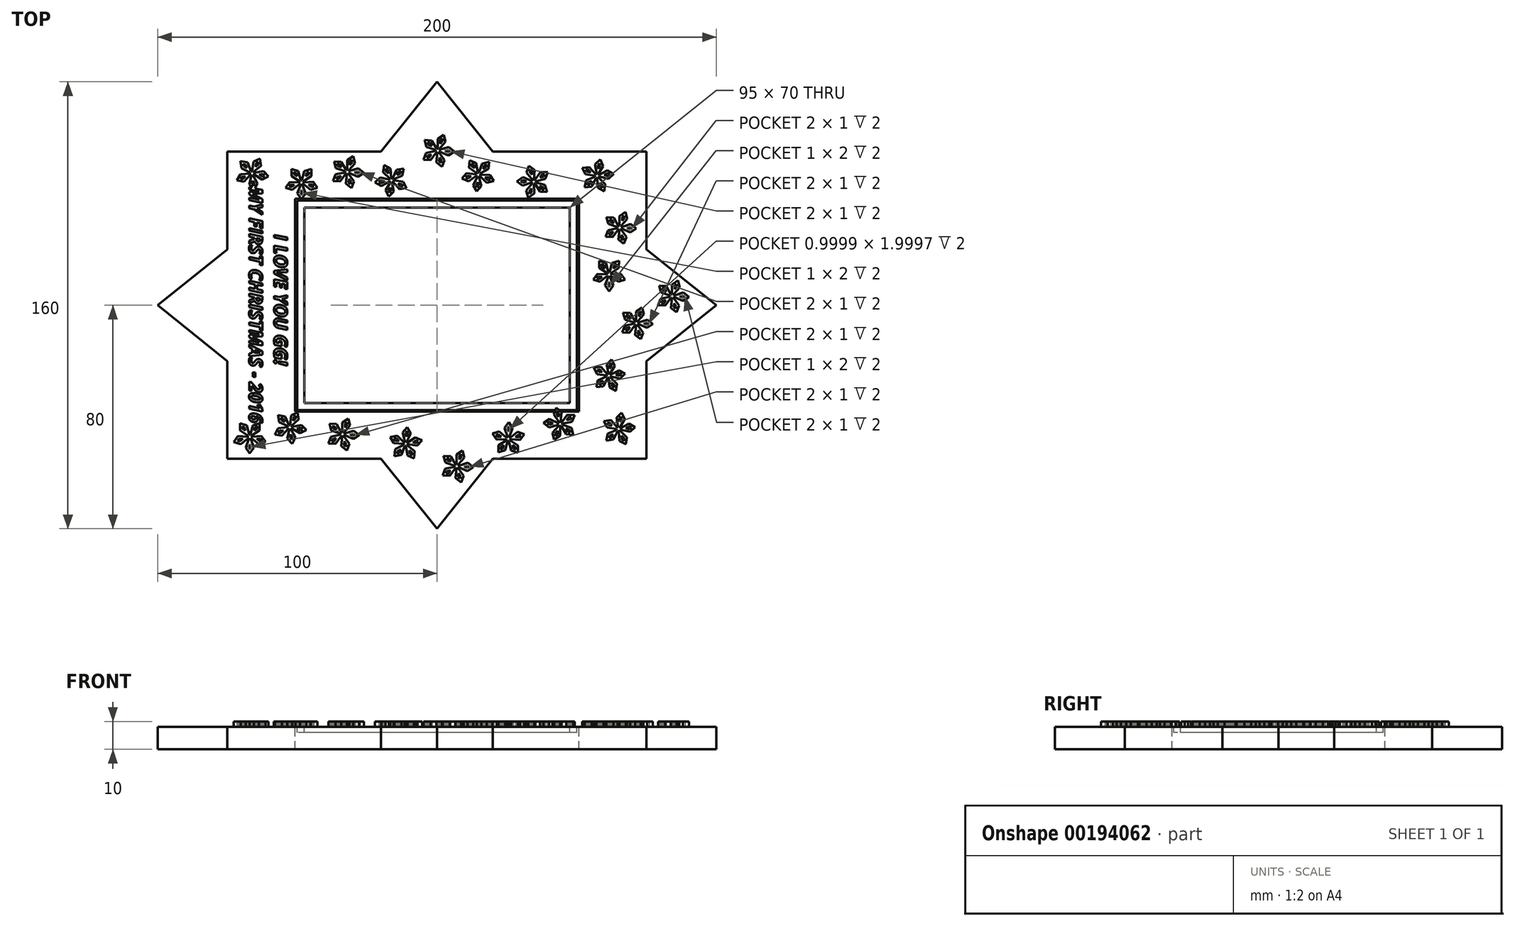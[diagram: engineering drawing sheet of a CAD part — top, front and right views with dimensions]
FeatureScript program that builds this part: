
annotation { "Feature Type Name" : "Feature", "Feature Type Description" : "" }
export const myFeature = defineFeature(function(context is Context, id is Id, definition is map)
    precondition{}
    {
        {
            var Q0;
            Q0=qCreatedBy(makeId("Top.planeOp"),FACE);
            var sketch = newSketch(context, id + "F0", { "sketchPlane" : qUnion([Q0])});
            skLineSegment(sketch, "E0.bottom", {"start": v(75, 55) * mm, "end": v(20, 55) * mm});
            skLineSegment(sketch, "E0.top", {"start": v(75, -55) * mm, "end": v(20, -55) * mm});
            skLineSegment(sketch, "E0.left", {"start": v(75, 55) * mm, "end": v(75, 20) * mm});
            skLineSegment(sketch, "E0.right", {"start": v(-75, 55) * mm, "end": v(-75, 20) * mm});
            skLineSegment(sketch, "E1", {"start": v(75, 20) * mm, "end": v(100, 0) * mm});
            skLineSegment(sketch, "E2", {"start": v(-20, 55) * mm, "end": v(0, 80) * mm});
            skLineSegment(sketch, "E3", {"start": v(0, 80) * mm, "end": v(20, 55) * mm});
            skLineSegment(sketch, "E4.MirrorCS", {"start": v(-20, -55) * mm, "end": v(0, -80) * mm});
            skLineSegment(sketch, "E5.MirrorCS", {"start": v(0, -80) * mm, "end": v(20, -55) * mm});
            skLineSegment(sketch, "E6.MirrorCS", {"start": v(75, -20) * mm, "end": v(100, 0) * mm});
            skLineSegment(sketch, "E7.MirrorCS", {"start": v(-75, 20) * mm, "end": v(-100, 0) * mm});
            skLineSegment(sketch, "E8.MirrorCS", {"start": v(-75, -20) * mm, "end": v(-100, 0) * mm});
            skLineSegment(sketch, "E9.trimOffspring", {"start": v(-75, -20) * mm, "end": v(-75, -55) * mm});
            skLineSegment(sketch, "E10.trimOffspring", {"start": v(75, -20) * mm, "end": v(75, -55) * mm});
            skLineSegment(sketch, "E11.trimOffspring", {"start": v(-20, -55) * mm, "end": v(-75, -55) * mm});
            skLineSegment(sketch, "E12.trimOffspring", {"start": v(-20, 55) * mm, "end": v(-75, 55) * mm});
            skPoint(sketch, "E13.MirrorCS.end.orphan", {"position": v(75, 34.57) * mm});
            skPoint(sketch, "E13.MirrorCS.start.orphan", {"position": v(100, 0) * mm});
            skPoint(sketch, "E14.orphan", {"position": v(75, -34.57) * mm});
            skSolve(sketch);
        }
        {
            var Q0;
            Q0=qSketchRegion(id+"F0",true);
            extrude(context, id + "F1", {"entities" : qUnion([Q0]), "endBound" : BoundingType.SYMMETRIC, "depth" : 8 * mm});
        }
        {
            var Q0;
            Q0=makeQuery(id+"F1.opExtrude","CAP_FACE",FACE,{"disambiguationData":[OSD([sQuery(id+"F0.wireOp",EDGE,"E0.bottom"),sQuery(id+"F0.wireOp",EDGE,"E0.top"),sQuery(id+"F0.wireOp",EDGE,"E0.left"),sQuery(id+"F0.wireOp",EDGE,"E0.right"),sQuery(id+"F0.wireOp",EDGE,"b7ca5f3b-2874-41bd-b902-1c79f96a0a8620.MirrorC"),sQuery(id+"F0.wireOp",EDGE,"b7ca5f3b-2874-41bd-b902-1c79f96a0a8621.MirrorC"),sQuery(id+"F0.wireOp",EDGE,"b7ca5f3b-2874-41bd-b902-1c79f96a0a8622.MirrorCS"),sQuery(id+"F0.wireOp",EDGE,"b7ca5f3b-2874-41bd-b902-1c79f96a0a8623.MirrorCS"),sQuery(id+"F0.wireOp",EDGE,"b7ca5f3b-2874-41bd-b902-1c79f96a0a8624.MirrorCS"),sQuery(id+"F0.wireOp",EDGE,"b7ca5f3b-2874-41bd-b902-1c79f96a0a8625.MirrorCS"),sQuery(id+"F0.wireOp",EDGE,"70034771-ba44-435e-ab74-29499f25fa1546.MirrorC"),sQuery(id+"F0.wireOp",EDGE,"70034771-ba44-435e-ab74-29499f25fa1547.MirrorCS"),sQuery(id+"F0.wireOp",EDGE,"70034771-ba44-435e-ab74-29499f25fa1548.MirrorC"),sQuery(id+"F0.wireOp",EDGE,"70034771-ba44-435e-ab74-29499f25fa1549.MirrorCS"),sQuery(id+"F0.wireOp",EDGE,"70034771-ba44-435e-ab74-29499f25fa1550.MirrorCS"),sQuery(id+"F0.wireOp",EDGE,"70034771-ba44-435e-ab74-29499f25fa1551.MirrorCS"),sQuery(id+"F0.wireOp",EDGE,"E1"),sQuery(id+"F0.wireOp",EDGE,"E2"),sQuery(id+"F0.wireOp",EDGE,"E3"),sQuery(id+"F0.wireOp",EDGE,"E4.MirrorCS"),sQuery(id+"F0.wireOp",EDGE,"E5.MirrorCS"),sQuery(id+"F0.wireOp",EDGE,"E6.MirrorCS"),sQuery(id+"F0.wireOp",EDGE,"E7.MirrorCS"),sQuery(id+"F0.wireOp",EDGE,"E8.MirrorCS"),sQuery(id+"F0.wireOp",EDGE,"E9.trimOffspring"),sQuery(id+"F0.wireOp",EDGE,"E10.trimOffspring"),sQuery(id+"F0.wireOp",EDGE,"E11.trimOffspring"),sQuery(id+"F0.wireOp",EDGE,"E12.trimOffspring")])],"isStart":false});
            var sketch = newSketch(context, id + "F2", { "sketchPlane" : qUnion([Q0])});
            skCircle(sketch, "E15.cCircle", {"center": v(65.31, 27.78) * mm, "radius": 6 * mm, "construction": true});
            skLineSegment(sketch, "E15.0", {"start": v(71.3, 27.48) * mm, "end": v(66.88, 22) * mm, "construction": true});
            skLineSegment(sketch, "E15.1", {"start": v(66.88, 22) * mm, "end": v(60.29, 24.5) * mm, "construction": true});
            skLineSegment(sketch, "E15.2", {"start": v(60.29, 24.5) * mm, "end": v(60.64, 31.55) * mm, "construction": true});
            skLineSegment(sketch, "E15.3", {"start": v(60.64, 31.55) * mm, "end": v(67.45, 33.39) * mm, "construction": true});
            skLineSegment(sketch, "E15.4", {"start": v(67.45, 33.39) * mm, "end": v(71.3, 27.48) * mm, "construction": true});
            skLineSegment(sketch, "E16", {"start": v(60.64, 31.55) * mm, "end": v(61.32, 29.08) * mm});
            skLineSegment(sketch, "E17", {"start": v(61.32, 29.08) * mm, "end": v(64.6, 28.02) * mm});
            skLineSegment(sketch, "E18", {"start": v(64.94, 28.43) * mm, "end": v(63.2, 31.42) * mm});
            skLineSegment(sketch, "E19", {"start": v(63.2, 31.42) * mm, "end": v(60.64, 31.55) * mm});
            skLineSegment(sketch, "E20", {"start": v(60.29, 24.5) * mm, "end": v(62.84, 24.38) * mm});
            skLineSegment(sketch, "E21", {"start": v(62.84, 24.38) * mm, "end": v(64.87, 27.18) * mm});
            skLineSegment(sketch, "E22", {"start": v(64.58, 27.63) * mm, "end": v(61.2, 26.9) * mm});
            skLineSegment(sketch, "E23", {"start": v(61.2, 26.9) * mm, "end": v(60.29, 24.5) * mm});
            skLineSegment(sketch, "E24", {"start": v(66.88, 22) * mm, "end": v(67.78, 24.38) * mm});
            skLineSegment(sketch, "E25", {"start": v(67.78, 24.38) * mm, "end": v(65.75, 27.18) * mm});
            skLineSegment(sketch, "E26", {"start": v(65.24, 27.04) * mm, "end": v(64.89, 23.6) * mm});
            skLineSegment(sketch, "E27", {"start": v(64.89, 23.6) * mm, "end": v(66.88, 22) * mm});
            skLineSegment(sketch, "E28", {"start": v(66, 27.48) * mm, "end": v(69.16, 26.09) * mm});
            skLineSegment(sketch, "E29", {"start": v(69.16, 26.09) * mm, "end": v(71.3, 27.48) * mm});
            skLineSegment(sketch, "E30", {"start": v(66.03, 28.02) * mm, "end": v(69.31, 29.08) * mm});
            skLineSegment(sketch, "E31", {"start": v(69.31, 29.08) * mm, "end": v(71.3, 27.48) * mm});
            skLineSegment(sketch, "E32", {"start": v(67.45, 33.39) * mm, "end": v(68.12, 30.92) * mm});
            skLineSegment(sketch, "E33", {"start": v(68.12, 30.92) * mm, "end": v(65.81, 28.34) * mm});
            skLineSegment(sketch, "E34", {"start": v(65.31, 28.53) * mm, "end": v(65.31, 31.99) * mm});
            skLineSegment(sketch, "E35", {"start": v(65.31, 31.99) * mm, "end": v(67.45, 33.39) * mm});
            skLineSegment(sketch, "E36", {"start": v(69.38, 30.43) * mm, "end": v(69.1, 24.74) * mm, "construction": true});
            skLineSegment(sketch, "E37", {"start": v(69.1, 24.74) * mm, "end": v(63.58, 23.25) * mm, "construction": true});
            skLineSegment(sketch, "E38", {"start": v(63.58, 23.25) * mm, "end": v(60.47, 28.03) * mm, "construction": true});
            skLineSegment(sketch, "E39", {"start": v(60.47, 28.03) * mm, "end": v(64.05, 32.47) * mm, "construction": true});
            skLineSegment(sketch, "E40", {"start": v(64.05, 32.47) * mm, "end": v(69.38, 30.43) * mm, "construction": true});
            skLineSegment(sketch, "E41", {"start": v(67.45, 33.39) * mm, "end": v(65.31, 27.78) * mm, "construction": true});
            skLineSegment(sketch, "E42", {"start": v(71.3, 27.48) * mm, "end": v(65.31, 27.78) * mm, "construction": true});
            skLineSegment(sketch, "E43", {"start": v(66.88, 22) * mm, "end": v(65.31, 27.78) * mm, "construction": true});
            skLineSegment(sketch, "E44", {"start": v(60.29, 24.5) * mm, "end": v(65.31, 27.78) * mm, "construction": true});
            skLineSegment(sketch, "E45", {"start": v(60.64, 31.55) * mm, "end": v(65.31, 27.78) * mm, "construction": true});
            skArc(sketch, "E46", {"start": v(64.87, 27.18) * mm, "mid": v(65.05, 27.08) * mm, "end": v(65.24, 27.04) * mm});
            skArc(sketch, "E47.trimOffspring", {"start": v(64.6, 28.02) * mm, "mid": v(64.56, 27.82) * mm, "end": v(64.58, 27.63) * mm});
            skArc(sketch, "E48.trimOffspring", {"start": v(65.31, 28.53) * mm, "mid": v(65.12, 28.5) * mm, "end": v(64.94, 28.43) * mm});
            skArc(sketch, "E49.trimOffspring", {"start": v(66.03, 28.02) * mm, "mid": v(65.94, 28.2) * mm, "end": v(65.81, 28.34) * mm});
            skArc(sketch, "E50.trimOffspring", {"start": v(65.75, 27.18) * mm, "mid": v(65.9, 27.31) * mm, "end": v(66, 27.48) * mm});
            skLineSegment(sketch, "E51", {"start": v(61.72, 30.68) * mm, "end": v(61.94, 29.86) * mm});
            skLineSegment(sketch, "E52", {"start": v(61.94, 29.86) * mm, "end": v(63.28, 29.43) * mm});
            skLineSegment(sketch, "E53", {"start": v(63.28, 29.43) * mm, "end": v(62.57, 30.64) * mm});
            skLineSegment(sketch, "E54", {"start": v(62.57, 30.64) * mm, "end": v(61.72, 30.68) * mm});
            skLineSegment(sketch, "E55", {"start": v(66.96, 32.1) * mm, "end": v(67.18, 31.27) * mm});
            skLineSegment(sketch, "E56", {"start": v(67.18, 31.27) * mm, "end": v(66.25, 30.23) * mm});
            skLineSegment(sketch, "E57", {"start": v(66.25, 30.23) * mm, "end": v(66.25, 31.63) * mm});
            skLineSegment(sketch, "E58", {"start": v(66.25, 31.63) * mm, "end": v(66.96, 32.1) * mm});
            skLineSegment(sketch, "E59", {"start": v(66.52, 23.33) * mm, "end": v(66.82, 24.12) * mm});
            skLineSegment(sketch, "E60", {"start": v(66.82, 24.12) * mm, "end": v(66, 25.26) * mm});
            skLineSegment(sketch, "E61", {"start": v(66, 25.26) * mm, "end": v(65.85, 23.86) * mm});
            skLineSegment(sketch, "E62", {"start": v(65.85, 23.86) * mm, "end": v(66.52, 23.33) * mm});
            skLineSegment(sketch, "E63", {"start": v(69.93, 27.55) * mm, "end": v(69.26, 28.09) * mm});
            skLineSegment(sketch, "E64", {"start": v(69.26, 28.09) * mm, "end": v(67.93, 27.65) * mm});
            skLineSegment(sketch, "E65", {"start": v(67.93, 27.65) * mm, "end": v(69.21, 27.09) * mm});
            skLineSegment(sketch, "E66", {"start": v(69.21, 27.09) * mm, "end": v(69.93, 27.55) * mm});
            skLineSegment(sketch, "E67", {"start": v(61.44, 25.26) * mm, "end": v(62.3, 25.22) * mm});
            skLineSegment(sketch, "E68", {"start": v(62.3, 25.22) * mm, "end": v(63.12, 26.35) * mm});
            skLineSegment(sketch, "E69", {"start": v(63.12, 26.35) * mm, "end": v(61.75, 26.06) * mm});
            skLineSegment(sketch, "E70", {"start": v(61.75, 26.06) * mm, "end": v(61.44, 25.26) * mm});
            skLineSegment(sketch, "E71", {"start": v(58.04, 15.9) * mm, "end": v(58.05, 13.34) * mm});
            skLineSegment(sketch, "E72", {"start": v(58.05, 13.34) * mm, "end": v(60.95, 11.46) * mm});
            skLineSegment(sketch, "E73", {"start": v(61.38, 11.77) * mm, "end": v(60.47, 15.1) * mm});
            skLineSegment(sketch, "E74", {"start": v(60.47, 15.1) * mm, "end": v(58.04, 15.9) * mm});
            skLineSegment(sketch, "E75", {"start": v(55.87, 9.19) * mm, "end": v(58.3, 8.4) * mm});
            skLineSegment(sketch, "E76", {"start": v(58.3, 8.4) * mm, "end": v(61, 10.58) * mm});
            skLineSegment(sketch, "E77", {"start": v(60.83, 11.09) * mm, "end": v(57.38, 11.26) * mm});
            skLineSegment(sketch, "E78", {"start": v(57.38, 11.26) * mm, "end": v(55.87, 9.19) * mm});
            skLineSegment(sketch, "E79", {"start": v(61.59, 5.05) * mm, "end": v(63.08, 7.13) * mm});
            skLineSegment(sketch, "E80", {"start": v(63.08, 7.13) * mm, "end": v(61.84, 10.35) * mm});
            skLineSegment(sketch, "E81", {"start": v(61.3, 10.35) * mm, "end": v(60.08, 7.12) * mm});
            skLineSegment(sketch, "E82", {"start": v(60.08, 7.12) * mm, "end": v(61.59, 5.05) * mm});
            skLineSegment(sketch, "E83", {"start": v(62.16, 10.58) * mm, "end": v(64.85, 8.42) * mm});
            skLineSegment(sketch, "E84", {"start": v(64.85, 8.42) * mm, "end": v(67.29, 9.2) * mm});
            skLineSegment(sketch, "E85", {"start": v(62.32, 11.09) * mm, "end": v(65.77, 11.27) * mm});
            skLineSegment(sketch, "E86", {"start": v(65.77, 11.27) * mm, "end": v(67.29, 9.2) * mm});
            skLineSegment(sketch, "E87", {"start": v(65.1, 15.9) * mm, "end": v(65.1, 13.35) * mm});
            skLineSegment(sketch, "E88", {"start": v(65.1, 13.35) * mm, "end": v(62.2, 11.46) * mm});
            skLineSegment(sketch, "E89", {"start": v(61.77, 11.77) * mm, "end": v(62.66, 15.11) * mm});
            skLineSegment(sketch, "E90", {"start": v(62.66, 15.11) * mm, "end": v(65.1, 15.9) * mm});
            skArc(sketch, "E91", {"start": v(61, 10.58) * mm, "mid": v(61.14, 10.44) * mm, "end": v(61.3, 10.35) * mm});
            skArc(sketch, "E92.trimOffspring", {"start": v(60.95, 11.46) * mm, "mid": v(60.86, 11.28) * mm, "end": v(60.83, 11.09) * mm});
            skArc(sketch, "E93.trimOffspring", {"start": v(61.77, 11.77) * mm, "mid": v(61.57, 11.8) * mm, "end": v(61.38, 11.77) * mm});
            skArc(sketch, "E94.trimOffspring", {"start": v(62.32, 11.09) * mm, "mid": v(62.29, 11.28) * mm, "end": v(62.2, 11.46) * mm});
            skArc(sketch, "E95.trimOffspring", {"start": v(61.84, 10.35) * mm, "mid": v(62.02, 10.44) * mm, "end": v(62.16, 10.58) * mm});
            skLineSegment(sketch, "E96", {"start": v(58.86, 14.78) * mm, "end": v(58.86, 13.93) * mm});
            skLineSegment(sketch, "E97", {"start": v(58.86, 13.93) * mm, "end": v(60.03, 13.17) * mm});
            skLineSegment(sketch, "E98", {"start": v(60.03, 13.17) * mm, "end": v(59.67, 14.52) * mm});
            skLineSegment(sketch, "E99", {"start": v(59.67, 14.52) * mm, "end": v(58.86, 14.78) * mm});
            skLineSegment(sketch, "E100", {"start": v(64.28, 14.8) * mm, "end": v(64.28, 13.94) * mm});
            skLineSegment(sketch, "E101", {"start": v(64.28, 13.94) * mm, "end": v(63.11, 13.17) * mm});
            skLineSegment(sketch, "E102", {"start": v(63.11, 13.17) * mm, "end": v(63.47, 14.52) * mm});
            skLineSegment(sketch, "E103", {"start": v(63.47, 14.52) * mm, "end": v(64.28, 14.8) * mm});
            skLineSegment(sketch, "E104", {"start": v(61.58, 6.43) * mm, "end": v(62.08, 7.12) * mm});
            skLineSegment(sketch, "E105", {"start": v(62.08, 7.12) * mm, "end": v(61.58, 8.43) * mm});
            skLineSegment(sketch, "E106", {"start": v(61.58, 8.43) * mm, "end": v(61.08, 7.12) * mm});
            skLineSegment(sketch, "E107", {"start": v(61.08, 7.12) * mm, "end": v(61.58, 6.43) * mm});
            skLineSegment(sketch, "E108", {"start": v(65.97, 9.63) * mm, "end": v(65.47, 10.32) * mm});
            skLineSegment(sketch, "E109", {"start": v(65.47, 10.32) * mm, "end": v(64.07, 10.25) * mm});
            skLineSegment(sketch, "E110", {"start": v(64.07, 10.25) * mm, "end": v(65.16, 9.37) * mm});
            skLineSegment(sketch, "E111", {"start": v(65.16, 9.37) * mm, "end": v(65.97, 9.63) * mm});
            skLineSegment(sketch, "E112", {"start": v(57.19, 9.62) * mm, "end": v(58, 9.35) * mm});
            skLineSegment(sketch, "E113", {"start": v(58, 9.35) * mm, "end": v(59.09, 10.24) * mm});
            skLineSegment(sketch, "E114", {"start": v(59.09, 10.24) * mm, "end": v(57.69, 10.3) * mm});
            skLineSegment(sketch, "E115", {"start": v(57.69, 10.3) * mm, "end": v(57.19, 9.62) * mm});
            skLineSegment(sketch, "E116", {"start": v(52, 49.2) * mm, "end": v(53.08, 46.88) * mm});
            skLineSegment(sketch, "E117", {"start": v(53.08, 46.88) * mm, "end": v(56.5, 46.4) * mm});
            skLineSegment(sketch, "E118", {"start": v(56.76, 46.87) * mm, "end": v(54.53, 49.5) * mm});
            skLineSegment(sketch, "E119", {"start": v(54.53, 49.5) * mm, "end": v(52, 49.2) * mm});
            skLineSegment(sketch, "E120", {"start": v(52.86, 42.2) * mm, "end": v(55.4, 42.52) * mm});
            skLineSegment(sketch, "E121", {"start": v(55.4, 42.52) * mm, "end": v(56.92, 45.62) * mm});
            skLineSegment(sketch, "E122", {"start": v(56.55, 46.01) * mm, "end": v(53.35, 44.7) * mm});
            skLineSegment(sketch, "E123", {"start": v(53.35, 44.7) * mm, "end": v(52.86, 42.2) * mm});
            skLineSegment(sketch, "E124", {"start": v(59.79, 40.86) * mm, "end": v(60.27, 43.37) * mm});
            skLineSegment(sketch, "E125", {"start": v(60.27, 43.37) * mm, "end": v(57.78, 45.77) * mm});
            skLineSegment(sketch, "E126", {"start": v(57.3, 45.55) * mm, "end": v(57.55, 42.1) * mm});
            skLineSegment(sketch, "E127", {"start": v(57.55, 42.1) * mm, "end": v(59.79, 40.86) * mm});
            skLineSegment(sketch, "E128", {"start": v(57.97, 46.12) * mm, "end": v(61.33, 45.3) * mm});
            skLineSegment(sketch, "E129", {"start": v(61.33, 45.3) * mm, "end": v(63.2, 47.04) * mm});
            skLineSegment(sketch, "E130", {"start": v(57.9, 46.65) * mm, "end": v(60.96, 48.27) * mm});
            skLineSegment(sketch, "E131", {"start": v(60.96, 48.27) * mm, "end": v(63.2, 47.04) * mm});
            skLineSegment(sketch, "E132", {"start": v(58.38, 52.19) * mm, "end": v(59.46, 49.87) * mm});
            skLineSegment(sketch, "E133", {"start": v(59.46, 49.87) * mm, "end": v(57.64, 46.93) * mm});
            skLineSegment(sketch, "E134", {"start": v(57.11, 47.03) * mm, "end": v(56.51, 50.43) * mm});
            skLineSegment(sketch, "E135", {"start": v(56.51, 50.43) * mm, "end": v(58.38, 52.19) * mm});
            skArc(sketch, "E136", {"start": v(56.92, 45.62) * mm, "mid": v(57.1, 45.56) * mm, "end": v(57.3, 45.55) * mm});
            skArc(sketch, "E137.trimOffspring", {"start": v(56.5, 46.4) * mm, "mid": v(56.5, 46.2) * mm, "end": v(56.55, 46.01) * mm});
            skArc(sketch, "E138.trimOffspring", {"start": v(57.11, 47.03) * mm, "mid": v(56.93, 46.97) * mm, "end": v(56.76, 46.87) * mm});
            skArc(sketch, "E139.trimOffspring", {"start": v(57.9, 46.65) * mm, "mid": v(57.8, 46.8) * mm, "end": v(57.64, 46.93) * mm});
            skArc(sketch, "E140.trimOffspring", {"start": v(57.78, 45.77) * mm, "mid": v(57.9, 45.93) * mm, "end": v(57.97, 46.12) * mm});
            skLineSegment(sketch, "E141", {"start": v(53.2, 48.53) * mm, "end": v(53.56, 47.76) * mm});
            skLineSegment(sketch, "E142", {"start": v(53.56, 47.76) * mm, "end": v(54.95, 47.56) * mm});
            skLineSegment(sketch, "E143", {"start": v(54.95, 47.56) * mm, "end": v(54.05, 48.63) * mm});
            skLineSegment(sketch, "E144", {"start": v(54.05, 48.63) * mm, "end": v(53.2, 48.53) * mm});
            skLineSegment(sketch, "E145", {"start": v(58.12, 50.83) * mm, "end": v(58.48, 50.06) * mm});
            skLineSegment(sketch, "E146", {"start": v(58.48, 50.06) * mm, "end": v(57.74, 48.87) * mm});
            skLineSegment(sketch, "E147", {"start": v(57.74, 48.87) * mm, "end": v(57.5, 50.25) * mm});
            skLineSegment(sketch, "E148", {"start": v(57.5, 50.25) * mm, "end": v(58.12, 50.83) * mm});
            skLineSegment(sketch, "E149", {"start": v(59.2, 42.11) * mm, "end": v(59.36, 42.95) * mm});
            skLineSegment(sketch, "E150", {"start": v(59.36, 42.95) * mm, "end": v(58.35, 43.92) * mm});
            skLineSegment(sketch, "E151", {"start": v(58.35, 43.92) * mm, "end": v(58.46, 42.53) * mm});
            skLineSegment(sketch, "E152", {"start": v(58.46, 42.53) * mm, "end": v(59.2, 42.11) * mm});
            skLineSegment(sketch, "E153", {"start": v(61.83, 46.87) * mm, "end": v(61.08, 47.28) * mm});
            skLineSegment(sketch, "E154", {"start": v(61.08, 47.28) * mm, "end": v(59.84, 46.62) * mm});
            skLineSegment(sketch, "E155", {"start": v(59.84, 46.62) * mm, "end": v(61.2, 46.28) * mm});
            skLineSegment(sketch, "E156", {"start": v(61.2, 46.28) * mm, "end": v(61.83, 46.87) * mm});
            skLineSegment(sketch, "E157", {"start": v(53.87, 43.14) * mm, "end": v(54.72, 43.25) * mm});
            skLineSegment(sketch, "E158", {"start": v(54.72, 43.25) * mm, "end": v(55.33, 44.5) * mm});
            skLineSegment(sketch, "E159", {"start": v(55.33, 44.5) * mm, "end": v(54.04, 43.98) * mm});
            skLineSegment(sketch, "E160", {"start": v(54.04, 43.98) * mm, "end": v(53.87, 43.14) * mm});
            skLineSegment(sketch, "E161", {"start": v(66.62, -2.64) * mm, "end": v(67.3, -5.1) * mm});
            skLineSegment(sketch, "E162", {"start": v(67.3, -5.1) * mm, "end": v(70.58, -6.18) * mm});
            skLineSegment(sketch, "E163", {"start": v(70.91, -5.76) * mm, "end": v(69.18, -2.77) * mm});
            skLineSegment(sketch, "E164", {"start": v(69.18, -2.77) * mm, "end": v(66.62, -2.64) * mm});
            skLineSegment(sketch, "E165", {"start": v(66.26, -9.68) * mm, "end": v(68.82, -9.8) * mm});
            skLineSegment(sketch, "E166", {"start": v(68.82, -9.8) * mm, "end": v(70.85, -7.02) * mm});
            skLineSegment(sketch, "E167", {"start": v(70.56, -6.57) * mm, "end": v(67.18, -7.3) * mm});
            skLineSegment(sketch, "E168", {"start": v(67.18, -7.3) * mm, "end": v(66.26, -9.68) * mm});
            skLineSegment(sketch, "E169", {"start": v(72.85, -12.2) * mm, "end": v(73.76, -9.8) * mm});
            skLineSegment(sketch, "E170", {"start": v(73.76, -9.8) * mm, "end": v(71.73, -7.02) * mm});
            skLineSegment(sketch, "E171", {"start": v(71.21, -7.15) * mm, "end": v(70.86, -10.6) * mm});
            skLineSegment(sketch, "E172", {"start": v(70.86, -10.6) * mm, "end": v(72.85, -12.2) * mm});
            skLineSegment(sketch, "E173", {"start": v(71.98, -6.71) * mm, "end": v(75.14, -8.1) * mm});
            skLineSegment(sketch, "E174", {"start": v(75.14, -8.1) * mm, "end": v(77.28, -6.71) * mm});
            skLineSegment(sketch, "E175", {"start": v(72, -6.18) * mm, "end": v(75.29, -5.1) * mm});
            skLineSegment(sketch, "E176", {"start": v(75.29, -5.1) * mm, "end": v(77.28, -6.71) * mm});
            skLineSegment(sketch, "E177", {"start": v(73.43, -0.8) * mm, "end": v(74.1, -3.28) * mm});
            skLineSegment(sketch, "E178", {"start": v(74.1, -3.28) * mm, "end": v(71.8, -5.85) * mm});
            skLineSegment(sketch, "E179", {"start": v(71.3, -5.66) * mm, "end": v(71.3, -2.2) * mm});
            skLineSegment(sketch, "E180", {"start": v(71.3, -2.2) * mm, "end": v(73.43, -0.8) * mm});
            skArc(sketch, "E181", {"start": v(70.85, -7.02) * mm, "mid": v(71.02, -7.1) * mm, "end": v(71.21, -7.15) * mm});
            skArc(sketch, "E182.trimOffspring", {"start": v(70.58, -6.18) * mm, "mid": v(70.54, -6.37) * mm, "end": v(70.56, -6.57) * mm});
            skArc(sketch, "E183.trimOffspring", {"start": v(71.3, -5.66) * mm, "mid": v(71.1, -5.68) * mm, "end": v(70.91, -5.76) * mm});
            skArc(sketch, "E184.trimOffspring", {"start": v(72, -6.18) * mm, "mid": v(71.92, -6) * mm, "end": v(71.8, -5.85) * mm});
            skArc(sketch, "E185.trimOffspring", {"start": v(71.73, -7.02) * mm, "mid": v(71.87, -6.88) * mm, "end": v(71.98, -6.71) * mm});
            skLineSegment(sketch, "E186", {"start": v(67.7, -3.5) * mm, "end": v(67.92, -4.33) * mm});
            skLineSegment(sketch, "E187", {"start": v(67.92, -4.33) * mm, "end": v(69.25, -4.76) * mm});
            skLineSegment(sketch, "E188", {"start": v(69.25, -4.76) * mm, "end": v(68.55, -3.55) * mm});
            skLineSegment(sketch, "E189", {"start": v(68.55, -3.55) * mm, "end": v(67.7, -3.5) * mm});
            skLineSegment(sketch, "E190", {"start": v(72.94, -2.1) * mm, "end": v(73.16, -2.92) * mm});
            skLineSegment(sketch, "E191", {"start": v(73.16, -2.92) * mm, "end": v(72.22, -3.96) * mm});
            skLineSegment(sketch, "E192", {"start": v(72.22, -3.96) * mm, "end": v(72.22, -2.56) * mm});
            skLineSegment(sketch, "E193", {"start": v(72.22, -2.56) * mm, "end": v(72.94, -2.1) * mm});
            skLineSegment(sketch, "E194", {"start": v(72.5, -10.87) * mm, "end": v(72.8, -10.07) * mm});
            skLineSegment(sketch, "E195", {"start": v(72.8, -10.07) * mm, "end": v(71.97, -8.94) * mm});
            skLineSegment(sketch, "E196", {"start": v(71.97, -8.94) * mm, "end": v(71.83, -10.33) * mm});
            skLineSegment(sketch, "E197", {"start": v(71.83, -10.33) * mm, "end": v(72.5, -10.87) * mm});
            skLineSegment(sketch, "E198", {"start": v(75.9, -6.64) * mm, "end": v(75.24, -6.1) * mm});
            skLineSegment(sketch, "E199", {"start": v(75.24, -6.1) * mm, "end": v(73.9, -6.54) * mm});
            skLineSegment(sketch, "E200", {"start": v(73.9, -6.54) * mm, "end": v(75.19, -7.1) * mm});
            skLineSegment(sketch, "E201", {"start": v(75.19, -7.1) * mm, "end": v(75.9, -6.64) * mm});
            skLineSegment(sketch, "E202", {"start": v(67.42, -8.93) * mm, "end": v(68.27, -8.97) * mm});
            skLineSegment(sketch, "E203", {"start": v(68.27, -8.97) * mm, "end": v(69.1, -7.84) * mm});
            skLineSegment(sketch, "E204", {"start": v(69.1, -7.84) * mm, "end": v(67.73, -8.13) * mm});
            skLineSegment(sketch, "E205", {"start": v(67.73, -8.13) * mm, "end": v(67.42, -8.93) * mm});
            skLineSegment(sketch, "E206", {"start": v(56.16, -22.34) * mm, "end": v(57.25, -24.66) * mm});
            skLineSegment(sketch, "E207", {"start": v(57.25, -24.66) * mm, "end": v(60.67, -25.14) * mm});
            skLineSegment(sketch, "E208", {"start": v(60.93, -24.67) * mm, "end": v(58.7, -22.03) * mm});
            skLineSegment(sketch, "E209", {"start": v(58.7, -22.03) * mm, "end": v(56.16, -22.34) * mm});
            skLineSegment(sketch, "E210", {"start": v(57.03, -29.34) * mm, "end": v(59.57, -29.02) * mm});
            skLineSegment(sketch, "E211", {"start": v(59.57, -29.02) * mm, "end": v(61.09, -25.92) * mm});
            skLineSegment(sketch, "E212", {"start": v(60.72, -25.53) * mm, "end": v(57.52, -26.83) * mm});
            skLineSegment(sketch, "E213", {"start": v(57.52, -26.83) * mm, "end": v(57.03, -29.34) * mm});
            skLineSegment(sketch, "E214", {"start": v(63.96, -30.68) * mm, "end": v(64.44, -28.16) * mm});
            skLineSegment(sketch, "E215", {"start": v(64.44, -28.16) * mm, "end": v(61.95, -25.76) * mm});
            skLineSegment(sketch, "E216", {"start": v(61.47, -26) * mm, "end": v(61.72, -29.44) * mm});
            skLineSegment(sketch, "E217", {"start": v(61.72, -29.44) * mm, "end": v(63.96, -30.68) * mm});
            skLineSegment(sketch, "E218", {"start": v(62.14, -25.42) * mm, "end": v(65.5, -26.25) * mm});
            skLineSegment(sketch, "E219", {"start": v(65.5, -26.25) * mm, "end": v(67.37, -24.5) * mm});
            skLineSegment(sketch, "E220", {"start": v(62.08, -24.9) * mm, "end": v(65.13, -23.27) * mm});
            skLineSegment(sketch, "E221", {"start": v(65.13, -23.27) * mm, "end": v(67.37, -24.5) * mm});
            skLineSegment(sketch, "E222", {"start": v(62.55, -19.35) * mm, "end": v(63.63, -21.67) * mm});
            skLineSegment(sketch, "E223", {"start": v(63.63, -21.67) * mm, "end": v(61.81, -24.6) * mm});
            skLineSegment(sketch, "E224", {"start": v(61.28, -24.5) * mm, "end": v(60.68, -21.1) * mm});
            skLineSegment(sketch, "E225", {"start": v(60.68, -21.1) * mm, "end": v(62.55, -19.35) * mm});
            skArc(sketch, "E226", {"start": v(61.09, -25.92) * mm, "mid": v(61.27, -25.98) * mm, "end": v(61.47, -26) * mm});
            skArc(sketch, "E227.trimOffspring", {"start": v(60.67, -25.14) * mm, "mid": v(60.67, -25.34) * mm, "end": v(60.72, -25.53) * mm});
            skArc(sketch, "E228.trimOffspring", {"start": v(61.28, -24.5) * mm, "mid": v(61.1, -24.56) * mm, "end": v(60.93, -24.67) * mm});
            skArc(sketch, "E229.trimOffspring", {"start": v(62.08, -24.9) * mm, "mid": v(61.96, -24.73) * mm, "end": v(61.81, -24.6) * mm});
            skArc(sketch, "E230.trimOffspring", {"start": v(61.95, -25.76) * mm, "mid": v(62.07, -25.6) * mm, "end": v(62.14, -25.42) * mm});
            skLineSegment(sketch, "E231", {"start": v(57.37, -23.01) * mm, "end": v(57.74, -23.78) * mm});
            skLineSegment(sketch, "E232", {"start": v(57.74, -23.78) * mm, "end": v(59.12, -23.98) * mm});
            skLineSegment(sketch, "E233", {"start": v(59.12, -23.98) * mm, "end": v(58.22, -22.9) * mm});
            skLineSegment(sketch, "E234", {"start": v(58.22, -22.9) * mm, "end": v(57.37, -23.01) * mm});
            skLineSegment(sketch, "E235", {"start": v(62.29, -20.7) * mm, "end": v(62.65, -21.48) * mm});
            skLineSegment(sketch, "E236", {"start": v(62.65, -21.48) * mm, "end": v(61.91, -22.67) * mm});
            skLineSegment(sketch, "E237", {"start": v(61.91, -22.67) * mm, "end": v(61.67, -21.3) * mm});
            skLineSegment(sketch, "E238", {"start": v(61.67, -21.3) * mm, "end": v(62.29, -20.7) * mm});
            skLineSegment(sketch, "E239", {"start": v(63.37, -29.42) * mm, "end": v(63.53, -28.59) * mm});
            skLineSegment(sketch, "E240", {"start": v(63.53, -28.59) * mm, "end": v(62.53, -27.61) * mm});
            skLineSegment(sketch, "E241", {"start": v(62.53, -27.61) * mm, "end": v(62.63, -29.01) * mm});
            skLineSegment(sketch, "E242", {"start": v(62.63, -29.01) * mm, "end": v(63.37, -29.42) * mm});
            skLineSegment(sketch, "E243", {"start": v(66, -24.67) * mm, "end": v(65.25, -24.26) * mm});
            skLineSegment(sketch, "E244", {"start": v(65.25, -24.26) * mm, "end": v(64.01, -24.92) * mm});
            skLineSegment(sketch, "E245", {"start": v(64.01, -24.92) * mm, "end": v(65.37, -25.25) * mm});
            skLineSegment(sketch, "E246", {"start": v(65.37, -25.25) * mm, "end": v(66, -24.67) * mm});
            skLineSegment(sketch, "E247", {"start": v(58.04, -28.4) * mm, "end": v(58.89, -28.3) * mm});
            skLineSegment(sketch, "E248", {"start": v(58.89, -28.3) * mm, "end": v(59.5, -27.03) * mm});
            skLineSegment(sketch, "E249", {"start": v(59.5, -27.03) * mm, "end": v(58.2, -27.56) * mm});
            skLineSegment(sketch, "E250", {"start": v(58.2, -27.56) * mm, "end": v(58.04, -28.4) * mm});
            skLineSegment(sketch, "E251", {"start": v(59.72, -41.45) * mm, "end": v(60.8, -43.76) * mm});
            skLineSegment(sketch, "E252", {"start": v(60.8, -43.76) * mm, "end": v(64.23, -44.24) * mm});
            skLineSegment(sketch, "E253", {"start": v(64.48, -43.77) * mm, "end": v(62.26, -41.13) * mm});
            skLineSegment(sketch, "E254", {"start": v(62.26, -41.13) * mm, "end": v(59.72, -41.45) * mm});
            skLineSegment(sketch, "E255", {"start": v(60.59, -48.44) * mm, "end": v(63.13, -48.12) * mm});
            skLineSegment(sketch, "E256", {"start": v(63.13, -48.12) * mm, "end": v(64.64, -45.02) * mm});
            skLineSegment(sketch, "E257", {"start": v(64.27, -44.63) * mm, "end": v(61.08, -45.93) * mm});
            skLineSegment(sketch, "E258", {"start": v(61.08, -45.93) * mm, "end": v(60.59, -48.44) * mm});
            skLineSegment(sketch, "E259", {"start": v(67.51, -49.78) * mm, "end": v(68, -47.27) * mm});
            skLineSegment(sketch, "E260", {"start": v(68, -47.27) * mm, "end": v(65.5, -44.87) * mm});
            skLineSegment(sketch, "E261", {"start": v(65.02, -45.1) * mm, "end": v(65.28, -48.54) * mm});
            skLineSegment(sketch, "E262", {"start": v(65.28, -48.54) * mm, "end": v(67.51, -49.78) * mm});
            skLineSegment(sketch, "E263", {"start": v(65.7, -44.52) * mm, "end": v(69.05, -45.35) * mm});
            skLineSegment(sketch, "E264", {"start": v(69.05, -45.35) * mm, "end": v(70.92, -43.6) * mm});
            skLineSegment(sketch, "E265", {"start": v(65.63, -44) * mm, "end": v(68.68, -42.37) * mm});
            skLineSegment(sketch, "E266", {"start": v(68.68, -42.37) * mm, "end": v(70.92, -43.6) * mm});
            skLineSegment(sketch, "E267", {"start": v(66.1, -38.45) * mm, "end": v(67.18, -40.77) * mm});
            skLineSegment(sketch, "E268", {"start": v(67.18, -40.77) * mm, "end": v(65.36, -43.7) * mm});
            skLineSegment(sketch, "E269", {"start": v(64.84, -43.6) * mm, "end": v(64.24, -40.2) * mm});
            skLineSegment(sketch, "E270", {"start": v(64.24, -40.2) * mm, "end": v(66.1, -38.45) * mm});
            skArc(sketch, "E271", {"start": v(64.64, -45.02) * mm, "mid": v(64.83, -45.08) * mm, "end": v(65.02, -45.1) * mm});
            skArc(sketch, "E272.trimOffspring", {"start": v(64.23, -44.24) * mm, "mid": v(64.22, -44.44) * mm, "end": v(64.27, -44.63) * mm});
            skArc(sketch, "E273.trimOffspring", {"start": v(64.84, -43.6) * mm, "mid": v(64.65, -43.67) * mm, "end": v(64.48, -43.77) * mm});
            skArc(sketch, "E274.trimOffspring", {"start": v(65.63, -44) * mm, "mid": v(65.52, -43.83) * mm, "end": v(65.36, -43.7) * mm});
            skArc(sketch, "E275.trimOffspring", {"start": v(65.5, -44.87) * mm, "mid": v(65.63, -44.7) * mm, "end": v(65.7, -44.52) * mm});
            skLineSegment(sketch, "E276", {"start": v(60.93, -42.11) * mm, "end": v(61.29, -42.89) * mm});
            skLineSegment(sketch, "E277", {"start": v(61.29, -42.89) * mm, "end": v(62.68, -43.08) * mm});
            skLineSegment(sketch, "E278", {"start": v(62.68, -43.08) * mm, "end": v(61.77, -42) * mm});
            skLineSegment(sketch, "E279", {"start": v(61.77, -42) * mm, "end": v(60.93, -42.11) * mm});
            skLineSegment(sketch, "E280", {"start": v(65.84, -39.81) * mm, "end": v(66.2, -40.58) * mm});
            skLineSegment(sketch, "E281", {"start": v(66.2, -40.58) * mm, "end": v(65.46, -41.77) * mm});
            skLineSegment(sketch, "E282", {"start": v(65.46, -41.77) * mm, "end": v(65.22, -40.4) * mm});
            skLineSegment(sketch, "E283", {"start": v(65.22, -40.4) * mm, "end": v(65.84, -39.81) * mm});
            skLineSegment(sketch, "E284", {"start": v(66.93, -48.53) * mm, "end": v(67.09, -47.7) * mm});
            skLineSegment(sketch, "E285", {"start": v(67.09, -47.7) * mm, "end": v(66.08, -46.72) * mm});
            skLineSegment(sketch, "E286", {"start": v(66.08, -46.72) * mm, "end": v(66.18, -48.11) * mm});
            skLineSegment(sketch, "E287", {"start": v(66.18, -48.11) * mm, "end": v(66.93, -48.53) * mm});
            skLineSegment(sketch, "E288", {"start": v(69.55, -43.78) * mm, "end": v(68.8, -43.36) * mm});
            skLineSegment(sketch, "E289", {"start": v(68.8, -43.36) * mm, "end": v(67.56, -44.02) * mm});
            skLineSegment(sketch, "E290", {"start": v(67.56, -44.02) * mm, "end": v(68.93, -44.36) * mm});
            skLineSegment(sketch, "E291", {"start": v(68.93, -44.36) * mm, "end": v(69.55, -43.78) * mm});
            skLineSegment(sketch, "E292", {"start": v(61.6, -47.5) * mm, "end": v(62.44, -47.4) * mm});
            skLineSegment(sketch, "E293", {"start": v(62.44, -47.4) * mm, "end": v(63.06, -46.13) * mm});
            skLineSegment(sketch, "E294", {"start": v(63.06, -46.13) * mm, "end": v(61.76, -46.66) * mm});
            skLineSegment(sketch, "E295", {"start": v(61.76, -46.66) * mm, "end": v(61.6, -47.5) * mm});
            skLineSegment(sketch, "E296", {"start": v(28.64, 44.39) * mm, "end": v(30.68, 42.84) * mm});
            skLineSegment(sketch, "E297", {"start": v(30.68, 42.84) * mm, "end": v(33.94, 44) * mm});
            skLineSegment(sketch, "E298", {"start": v(33.95, 44.54) * mm, "end": v(30.75, 45.84) * mm});
            skLineSegment(sketch, "E299", {"start": v(30.75, 45.84) * mm, "end": v(28.64, 44.39) * mm});
            skLineSegment(sketch, "E300", {"start": v(32.66, 38.6) * mm, "end": v(34.76, 40.06) * mm});
            skLineSegment(sketch, "E301", {"start": v(34.76, 40.06) * mm, "end": v(34.66, 43.5) * mm});
            skLineSegment(sketch, "E302", {"start": v(34.16, 43.68) * mm, "end": v(31.93, 41.04) * mm});
            skLineSegment(sketch, "E303", {"start": v(31.93, 41.04) * mm, "end": v(32.66, 38.6) * mm});
            skLineSegment(sketch, "E304", {"start": v(39.42, 40.62) * mm, "end": v(38.68, 43.07) * mm});
            skLineSegment(sketch, "E305", {"start": v(38.68, 43.07) * mm, "end": v(35.36, 44.05) * mm});
            skLineSegment(sketch, "E306", {"start": v(35.04, 43.62) * mm, "end": v(36.86, 40.69) * mm});
            skLineSegment(sketch, "E307", {"start": v(36.86, 40.69) * mm, "end": v(39.42, 40.62) * mm});
            skLineSegment(sketch, "E308", {"start": v(35.37, 44.44) * mm, "end": v(38.72, 45.26) * mm});
            skLineSegment(sketch, "E309", {"start": v(38.72, 45.26) * mm, "end": v(39.57, 47.68) * mm});
            skLineSegment(sketch, "E310", {"start": v(35.07, 44.88) * mm, "end": v(37.01, 47.73) * mm});
            skLineSegment(sketch, "E311", {"start": v(37.01, 47.73) * mm, "end": v(39.57, 47.68) * mm});
            skLineSegment(sketch, "E312", {"start": v(32.91, 50) * mm, "end": v(34.95, 48.45) * mm});
            skLineSegment(sketch, "E313", {"start": v(34.95, 48.45) * mm, "end": v(34.7, 45) * mm});
            skLineSegment(sketch, "E314", {"start": v(34.18, 44.85) * mm, "end": v(32.07, 47.59) * mm});
            skLineSegment(sketch, "E315", {"start": v(32.07, 47.59) * mm, "end": v(32.91, 50) * mm});
            skArc(sketch, "E316", {"start": v(34.66, 43.5) * mm, "mid": v(34.86, 43.54) * mm, "end": v(35.04, 43.62) * mm});
            skArc(sketch, "E317.trimOffspring", {"start": v(33.94, 44) * mm, "mid": v(34.03, 43.83) * mm, "end": v(34.16, 43.68) * mm});
            skArc(sketch, "E318.trimOffspring", {"start": v(34.18, 44.85) * mm, "mid": v(34.05, 44.71) * mm, "end": v(33.95, 44.54) * mm});
            skArc(sketch, "E319.trimOffspring", {"start": v(35.07, 44.88) * mm, "mid": v(34.89, 44.97) * mm, "end": v(34.7, 45) * mm});
            skArc(sketch, "E320.trimOffspring", {"start": v(35.36, 44.05) * mm, "mid": v(35.4, 44.24) * mm, "end": v(35.37, 44.44) * mm});
            skLineSegment(sketch, "E321", {"start": v(30.03, 44.36) * mm, "end": v(30.7, 43.84) * mm});
            skLineSegment(sketch, "E322", {"start": v(30.7, 43.84) * mm, "end": v(32.02, 44.31) * mm});
            skLineSegment(sketch, "E323", {"start": v(32.02, 44.31) * mm, "end": v(30.73, 44.84) * mm});
            skLineSegment(sketch, "E324", {"start": v(30.73, 44.84) * mm, "end": v(30.03, 44.36) * mm});
            skLineSegment(sketch, "E325", {"start": v(33.31, 48.68) * mm, "end": v(33.99, 48.16) * mm});
            skLineSegment(sketch, "E326", {"start": v(33.99, 48.16) * mm, "end": v(33.89, 46.76) * mm});
            skLineSegment(sketch, "E327", {"start": v(33.89, 46.76) * mm, "end": v(33.03, 47.87) * mm});
            skLineSegment(sketch, "E328", {"start": v(33.03, 47.87) * mm, "end": v(33.31, 48.68) * mm});
            skLineSegment(sketch, "E329", {"start": v(38.32, 41.46) * mm, "end": v(38.07, 42.28) * mm});
            skLineSegment(sketch, "E330", {"start": v(38.07, 42.28) * mm, "end": v(36.73, 42.67) * mm});
            skLineSegment(sketch, "E331", {"start": v(36.73, 42.67) * mm, "end": v(37.46, 41.48) * mm});
            skLineSegment(sketch, "E332", {"start": v(37.46, 41.48) * mm, "end": v(38.32, 41.46) * mm});
            skLineSegment(sketch, "E333", {"start": v(38.44, 46.89) * mm, "end": v(37.58, 46.9) * mm});
            skLineSegment(sketch, "E334", {"start": v(37.58, 46.9) * mm, "end": v(36.8, 45.75) * mm});
            skLineSegment(sketch, "E335", {"start": v(36.8, 45.75) * mm, "end": v(38.15, 46.08) * mm});
            skLineSegment(sketch, "E336", {"start": v(38.15, 46.08) * mm, "end": v(38.44, 46.89) * mm});
            skLineSegment(sketch, "E337", {"start": v(33.12, 39.9) * mm, "end": v(33.82, 40.39) * mm});
            skLineSegment(sketch, "E338", {"start": v(33.82, 40.39) * mm, "end": v(33.78, 41.79) * mm});
            skLineSegment(sketch, "E339", {"start": v(33.78, 41.79) * mm, "end": v(32.87, 40.71) * mm});
            skLineSegment(sketch, "E340", {"start": v(32.87, 40.71) * mm, "end": v(33.12, 39.9) * mm});
            skLineSegment(sketch, "E341", {"start": v(-4.44, 59.17) * mm, "end": v(-3.77, 56.7) * mm});
            skLineSegment(sketch, "E342", {"start": v(-3.77, 56.7) * mm, "end": v(-0.49, 55.64) * mm});
            skLineSegment(sketch, "E343", {"start": v(-0.15, 56.05) * mm, "end": v(-1.89, 59.04) * mm});
            skLineSegment(sketch, "E344", {"start": v(-1.89, 59.04) * mm, "end": v(-4.44, 59.17) * mm});
            skLineSegment(sketch, "E345", {"start": v(-4.8, 52.13) * mm, "end": v(-2.24, 52) * mm});
            skLineSegment(sketch, "E346", {"start": v(-2.24, 52) * mm, "end": v(-0.21, 54.8) * mm});
            skLineSegment(sketch, "E347", {"start": v(-0.5, 55.25) * mm, "end": v(-3.88, 54.52) * mm});
            skLineSegment(sketch, "E348", {"start": v(-3.88, 54.52) * mm, "end": v(-4.8, 52.13) * mm});
            skLineSegment(sketch, "E349", {"start": v(1.79, 49.61) * mm, "end": v(2.7, 52) * mm});
            skLineSegment(sketch, "E350", {"start": v(2.7, 52) * mm, "end": v(0.67, 54.8) * mm});
            skLineSegment(sketch, "E351", {"start": v(0.15, 54.66) * mm, "end": v(-0.2, 51.22) * mm});
            skLineSegment(sketch, "E352", {"start": v(-0.2, 51.22) * mm, "end": v(1.79, 49.61) * mm});
            skLineSegment(sketch, "E353", {"start": v(0.91, 55.1) * mm, "end": v(4.07, 53.7) * mm});
            skLineSegment(sketch, "E354", {"start": v(4.07, 53.7) * mm, "end": v(6.22, 55.1) * mm});
            skLineSegment(sketch, "E355", {"start": v(0.94, 55.64) * mm, "end": v(4.22, 56.7) * mm});
            skLineSegment(sketch, "E356", {"start": v(4.22, 56.7) * mm, "end": v(6.22, 55.1) * mm});
            skLineSegment(sketch, "E357", {"start": v(2.37, 61.01) * mm, "end": v(3.03, 58.54) * mm});
            skLineSegment(sketch, "E358", {"start": v(3.03, 58.54) * mm, "end": v(0.73, 55.96) * mm});
            skLineSegment(sketch, "E359", {"start": v(0.23, 56.16) * mm, "end": v(0.23, 59.6) * mm});
            skLineSegment(sketch, "E360", {"start": v(0.23, 59.6) * mm, "end": v(2.37, 61.01) * mm});
            skArc(sketch, "E361", {"start": v(-0.21, 54.8) * mm, "mid": v(-0.04, 54.7) * mm, "end": v(0.15, 54.66) * mm});
            skArc(sketch, "E362.trimOffspring", {"start": v(-0.49, 55.64) * mm, "mid": v(-0.52, 55.44) * mm, "end": v(-0.5, 55.25) * mm});
            skArc(sketch, "E363.trimOffspring", {"start": v(0.23, 56.16) * mm, "mid": v(0.03, 56.13) * mm, "end": v(-0.15, 56.05) * mm});
            skArc(sketch, "E364.trimOffspring", {"start": v(0.94, 55.64) * mm, "mid": v(0.85, 55.82) * mm, "end": v(0.73, 55.96) * mm});
            skArc(sketch, "E365.trimOffspring", {"start": v(0.67, 54.8) * mm, "mid": v(0.81, 54.93) * mm, "end": v(0.91, 55.1) * mm});
            skLineSegment(sketch, "E366", {"start": v(-3.37, 58.3) * mm, "end": v(-3.14, 57.48) * mm});
            skLineSegment(sketch, "E367", {"start": v(-3.14, 57.48) * mm, "end": v(-1.81, 57.05) * mm});
            skLineSegment(sketch, "E368", {"start": v(-1.81, 57.05) * mm, "end": v(-2.52, 58.26) * mm});
            skLineSegment(sketch, "E369", {"start": v(-2.52, 58.26) * mm, "end": v(-3.37, 58.3) * mm});
            skLineSegment(sketch, "E370", {"start": v(1.87, 59.72) * mm, "end": v(2.1, 58.9) * mm});
            skLineSegment(sketch, "E371", {"start": v(2.1, 58.9) * mm, "end": v(1.16, 57.85) * mm});
            skLineSegment(sketch, "E372", {"start": v(1.16, 57.85) * mm, "end": v(1.16, 59.25) * mm});
            skLineSegment(sketch, "E373", {"start": v(1.16, 59.25) * mm, "end": v(1.87, 59.72) * mm});
            skLineSegment(sketch, "E374", {"start": v(1.43, 50.95) * mm, "end": v(1.73, 51.74) * mm});
            skLineSegment(sketch, "E375", {"start": v(1.73, 51.74) * mm, "end": v(0.9, 52.88) * mm});
            skLineSegment(sketch, "E376", {"start": v(0.9, 52.88) * mm, "end": v(0.77, 51.48) * mm});
            skLineSegment(sketch, "E377", {"start": v(0.77, 51.48) * mm, "end": v(1.43, 50.95) * mm});
            skLineSegment(sketch, "E378", {"start": v(4.84, 55.17) * mm, "end": v(4.17, 55.7) * mm});
            skLineSegment(sketch, "E379", {"start": v(4.17, 55.7) * mm, "end": v(2.84, 55.27) * mm});
            skLineSegment(sketch, "E380", {"start": v(2.84, 55.27) * mm, "end": v(4.12, 54.7) * mm});
            skLineSegment(sketch, "E381", {"start": v(4.12, 54.7) * mm, "end": v(4.84, 55.17) * mm});
            skLineSegment(sketch, "E382", {"start": v(-3.64, 52.88) * mm, "end": v(-2.8, 52.84) * mm});
            skLineSegment(sketch, "E383", {"start": v(-2.8, 52.84) * mm, "end": v(-1.97, 53.98) * mm});
            skLineSegment(sketch, "E384", {"start": v(-1.97, 53.98) * mm, "end": v(-3.34, 53.68) * mm});
            skLineSegment(sketch, "E385", {"start": v(-3.34, 53.68) * mm, "end": v(-3.64, 52.88) * mm});
            skLineSegment(sketch, "E386", {"start": v(8.94, 45.4) * mm, "end": v(11.3, 44.43) * mm});
            skLineSegment(sketch, "E387", {"start": v(11.3, 44.43) * mm, "end": v(14.16, 46.37) * mm});
            skLineSegment(sketch, "E388", {"start": v(14.03, 46.89) * mm, "end": v(10.6, 47.34) * mm});
            skLineSegment(sketch, "E389", {"start": v(10.6, 47.34) * mm, "end": v(8.94, 45.4) * mm});
            skLineSegment(sketch, "E390", {"start": v(14.29, 40.81) * mm, "end": v(15.95, 42.75) * mm});
            skLineSegment(sketch, "E391", {"start": v(15.95, 42.75) * mm, "end": v(14.98, 46.07) * mm});
            skLineSegment(sketch, "E392", {"start": v(14.45, 46.11) * mm, "end": v(12.96, 43) * mm});
            skLineSegment(sketch, "E393", {"start": v(12.96, 43) * mm, "end": v(14.29, 40.81) * mm});
            skLineSegment(sketch, "E394", {"start": v(20.31, 44.48) * mm, "end": v(18.98, 46.66) * mm});
            skLineSegment(sketch, "E395", {"start": v(18.98, 46.66) * mm, "end": v(15.52, 46.77) * mm});
            skLineSegment(sketch, "E396", {"start": v(15.32, 46.27) * mm, "end": v(17.82, 43.9) * mm});
            skLineSegment(sketch, "E397", {"start": v(17.82, 43.9) * mm, "end": v(20.31, 44.48) * mm});
            skLineSegment(sketch, "E398", {"start": v(15.43, 47.15) * mm, "end": v(18.47, 48.8) * mm});
            skLineSegment(sketch, "E399", {"start": v(18.47, 48.8) * mm, "end": v(18.68, 51.34) * mm});
            skLineSegment(sketch, "E400", {"start": v(15.03, 47.5) * mm, "end": v(16.2, 50.75) * mm});
            skLineSegment(sketch, "E401", {"start": v(16.2, 50.75) * mm, "end": v(18.68, 51.34) * mm});
            skLineSegment(sketch, "E402", {"start": v(11.65, 51.92) * mm, "end": v(14.01, 50.93) * mm});
            skLineSegment(sketch, "E403", {"start": v(14.01, 50.93) * mm, "end": v(14.64, 47.53) * mm});
            skLineSegment(sketch, "E404", {"start": v(14.18, 47.25) * mm, "end": v(11.45, 49.36) * mm});
            skLineSegment(sketch, "E405", {"start": v(11.45, 49.36) * mm, "end": v(11.65, 51.92) * mm});
            skArc(sketch, "E406", {"start": v(14.98, 46.07) * mm, "mid": v(15.17, 46.15) * mm, "end": v(15.32, 46.27) * mm});
            skArc(sketch, "E407.trimOffspring", {"start": v(14.16, 46.37) * mm, "mid": v(14.29, 46.22) * mm, "end": v(14.45, 46.11) * mm});
            skArc(sketch, "E408.trimOffspring", {"start": v(14.18, 47.25) * mm, "mid": v(14.08, 47.08) * mm, "end": v(14.03, 46.89) * mm});
            skArc(sketch, "E409.trimOffspring", {"start": v(15.03, 47.5) * mm, "mid": v(14.84, 47.54) * mm, "end": v(14.64, 47.53) * mm});
            skArc(sketch, "E410.trimOffspring", {"start": v(15.52, 46.77) * mm, "mid": v(15.5, 46.96) * mm, "end": v(15.43, 47.15) * mm});
            skLineSegment(sketch, "E411", {"start": v(10.28, 45.73) * mm, "end": v(11.07, 45.4) * mm});
            skLineSegment(sketch, "E412", {"start": v(11.07, 45.4) * mm, "end": v(12.23, 46.19) * mm});
            skLineSegment(sketch, "E413", {"start": v(12.23, 46.19) * mm, "end": v(10.84, 46.37) * mm});
            skLineSegment(sketch, "E414", {"start": v(10.84, 46.37) * mm, "end": v(10.28, 45.73) * mm});
            skLineSegment(sketch, "E415", {"start": v(12.37, 50.74) * mm, "end": v(13.16, 50.4) * mm});
            skLineSegment(sketch, "E416", {"start": v(13.16, 50.4) * mm, "end": v(13.41, 49.03) * mm});
            skLineSegment(sketch, "E417", {"start": v(13.41, 49.03) * mm, "end": v(12.3, 49.88) * mm});
            skLineSegment(sketch, "E418", {"start": v(12.3, 49.88) * mm, "end": v(12.37, 50.74) * mm});
            skLineSegment(sketch, "E419", {"start": v(19.04, 45.01) * mm, "end": v(18.6, 45.74) * mm});
            skLineSegment(sketch, "E420", {"start": v(18.6, 45.74) * mm, "end": v(17.2, 45.78) * mm});
            skLineSegment(sketch, "E421", {"start": v(17.2, 45.78) * mm, "end": v(18.2, 44.82) * mm});
            skLineSegment(sketch, "E422", {"start": v(18.2, 44.82) * mm, "end": v(19.04, 45.01) * mm});
            skLineSegment(sketch, "E423", {"start": v(17.78, 50.3) * mm, "end": v(16.95, 50.1) * mm});
            skLineSegment(sketch, "E424", {"start": v(16.95, 50.1) * mm, "end": v(16.48, 48.78) * mm});
            skLineSegment(sketch, "E425", {"start": v(16.48, 48.78) * mm, "end": v(17.71, 49.44) * mm});
            skLineSegment(sketch, "E426", {"start": v(17.71, 49.44) * mm, "end": v(17.78, 50.3) * mm});
            skLineSegment(sketch, "E427", {"start": v(14.4, 42.19) * mm, "end": v(14.95, 42.84) * mm});
            skLineSegment(sketch, "E428", {"start": v(14.95, 42.84) * mm, "end": v(14.56, 44.18) * mm});
            skLineSegment(sketch, "E429", {"start": v(14.56, 44.18) * mm, "end": v(13.96, 42.92) * mm});
            skLineSegment(sketch, "E430", {"start": v(13.96, 42.92) * mm, "end": v(14.4, 42.19) * mm});
            skLineSegment(sketch, "E431", {"start": v(19.84, -45.96) * mm, "end": v(21.32, -48.05) * mm});
            skLineSegment(sketch, "E432", {"start": v(21.32, -48.05) * mm, "end": v(24.77, -47.93) * mm});
            skLineSegment(sketch, "E433", {"start": v(24.94, -47.42) * mm, "end": v(22.29, -45.21) * mm});
            skLineSegment(sketch, "E434", {"start": v(22.29, -45.21) * mm, "end": v(19.84, -45.96) * mm});
            skLineSegment(sketch, "E435", {"start": v(21.91, -52.7) * mm, "end": v(24.36, -51.94) * mm});
            skLineSegment(sketch, "E436", {"start": v(24.36, -51.94) * mm, "end": v(25.31, -48.62) * mm});
            skLineSegment(sketch, "E437", {"start": v(24.88, -48.3) * mm, "end": v(21.96, -50.14) * mm});
            skLineSegment(sketch, "E438", {"start": v(21.96, -50.14) * mm, "end": v(21.91, -52.7) * mm});
            skLineSegment(sketch, "E439", {"start": v(28.97, -52.81) * mm, "end": v(29, -50.25) * mm});
            skLineSegment(sketch, "E440", {"start": v(29, -50.25) * mm, "end": v(26.14, -48.32) * mm});
            skLineSegment(sketch, "E441", {"start": v(25.7, -48.63) * mm, "end": v(26.55, -51.98) * mm});
            skLineSegment(sketch, "E442", {"start": v(26.55, -51.98) * mm, "end": v(28.97, -52.81) * mm});
            skLineSegment(sketch, "E443", {"start": v(26.27, -47.95) * mm, "end": v(29.71, -48.18) * mm});
            skLineSegment(sketch, "E444", {"start": v(29.71, -48.18) * mm, "end": v(31.25, -46.14) * mm});
            skLineSegment(sketch, "E445", {"start": v(26.1, -47.44) * mm, "end": v(28.83, -45.31) * mm});
            skLineSegment(sketch, "E446", {"start": v(28.83, -45.31) * mm, "end": v(31.25, -46.14) * mm});
            skLineSegment(sketch, "E447", {"start": v(25.61, -41.9) * mm, "end": v(27.08, -44) * mm});
            skLineSegment(sketch, "E448", {"start": v(27.08, -44) * mm, "end": v(25.8, -47.2) * mm});
            skLineSegment(sketch, "E449", {"start": v(25.26, -47.2) * mm, "end": v(24.08, -43.95) * mm});
            skLineSegment(sketch, "E450", {"start": v(24.08, -43.95) * mm, "end": v(25.61, -41.9) * mm});
            skArc(sketch, "E451", {"start": v(25.31, -48.62) * mm, "mid": v(25.5, -48.65) * mm, "end": v(25.7, -48.63) * mm});
            skArc(sketch, "E452.trimOffspring", {"start": v(24.77, -47.93) * mm, "mid": v(24.8, -48.12) * mm, "end": v(24.88, -48.3) * mm});
            skArc(sketch, "E453.trimOffspring", {"start": v(25.26, -47.2) * mm, "mid": v(25.09, -47.29) * mm, "end": v(24.94, -47.42) * mm});
            skArc(sketch, "E454.trimOffspring", {"start": v(26.1, -47.44) * mm, "mid": v(25.97, -47.3) * mm, "end": v(25.8, -47.2) * mm});
            skArc(sketch, "E455.trimOffspring", {"start": v(26.14, -48.32) * mm, "mid": v(26.23, -48.15) * mm, "end": v(26.27, -47.95) * mm});
            skLineSegment(sketch, "E456", {"start": v(21.15, -46.4) * mm, "end": v(21.64, -47.1) * mm});
            skLineSegment(sketch, "E457", {"start": v(21.64, -47.1) * mm, "end": v(23.04, -47.05) * mm});
            skLineSegment(sketch, "E458", {"start": v(23.04, -47.05) * mm, "end": v(21.96, -46.16) * mm});
            skLineSegment(sketch, "E459", {"start": v(21.96, -46.16) * mm, "end": v(21.15, -46.4) * mm});
            skLineSegment(sketch, "E460", {"start": v(25.6, -43.28) * mm, "end": v(26.08, -43.98) * mm});
            skLineSegment(sketch, "E461", {"start": v(26.08, -43.98) * mm, "end": v(25.56, -45.28) * mm});
            skLineSegment(sketch, "E462", {"start": v(25.56, -45.28) * mm, "end": v(25.08, -43.97) * mm});
            skLineSegment(sketch, "E463", {"start": v(25.08, -43.97) * mm, "end": v(25.6, -43.28) * mm});
            skLineSegment(sketch, "E464", {"start": v(28.17, -51.68) * mm, "end": v(28.18, -50.83) * mm});
            skLineSegment(sketch, "E465", {"start": v(28.18, -50.83) * mm, "end": v(27.02, -50.04) * mm});
            skLineSegment(sketch, "E466", {"start": v(27.02, -50.04) * mm, "end": v(27.37, -51.4) * mm});
            skLineSegment(sketch, "E467", {"start": v(27.37, -51.4) * mm, "end": v(28.17, -51.68) * mm});
            skLineSegment(sketch, "E468", {"start": v(29.93, -46.54) * mm, "end": v(29.12, -46.27) * mm});
            skLineSegment(sketch, "E469", {"start": v(29.12, -46.27) * mm, "end": v(28.02, -47.13) * mm});
            skLineSegment(sketch, "E470", {"start": v(28.02, -47.13) * mm, "end": v(29.42, -47.23) * mm});
            skLineSegment(sketch, "E471", {"start": v(29.42, -47.23) * mm, "end": v(29.93, -46.54) * mm});
            skLineSegment(sketch, "E472", {"start": v(22.74, -51.6) * mm, "end": v(23.56, -51.34) * mm});
            skLineSegment(sketch, "E473", {"start": v(23.56, -51.34) * mm, "end": v(23.95, -50) * mm});
            skLineSegment(sketch, "E474", {"start": v(23.95, -50) * mm, "end": v(22.76, -50.74) * mm});
            skLineSegment(sketch, "E475", {"start": v(22.76, -50.74) * mm, "end": v(22.74, -51.6) * mm});
            skLineSegment(sketch, "E476", {"start": v(-18.89, 50.19) * mm, "end": v(-19.32, 47.66) * mm});
            skLineSegment(sketch, "E477", {"start": v(-19.32, 47.66) * mm, "end": v(-16.8, 45.3) * mm});
            skLineSegment(sketch, "E478", {"start": v(-16.32, 45.54) * mm, "end": v(-16.63, 48.98) * mm});
            skLineSegment(sketch, "E479", {"start": v(-16.63, 48.98) * mm, "end": v(-18.89, 50.19) * mm});
            skLineSegment(sketch, "E480", {"start": v(-22.19, 43.95) * mm, "end": v(-19.92, 42.76) * mm});
            skLineSegment(sketch, "E481", {"start": v(-19.92, 42.76) * mm, "end": v(-16.9, 44.43) * mm});
            skLineSegment(sketch, "E482", {"start": v(-16.98, 44.96) * mm, "end": v(-20.35, 45.73) * mm});
            skLineSegment(sketch, "E483", {"start": v(-20.35, 45.73) * mm, "end": v(-22.19, 43.95) * mm});
            skLineSegment(sketch, "E484", {"start": v(-17.28, 38.89) * mm, "end": v(-15.45, 40.67) * mm});
            skLineSegment(sketch, "E485", {"start": v(-15.45, 40.67) * mm, "end": v(-16.1, 44.06) * mm});
            skLineSegment(sketch, "E486", {"start": v(-16.63, 44.15) * mm, "end": v(-18.4, 41.19) * mm});
            skLineSegment(sketch, "E487", {"start": v(-18.4, 41.19) * mm, "end": v(-17.28, 38.89) * mm});
            skLineSegment(sketch, "E488", {"start": v(-15.75, 44.23) * mm, "end": v(-13.48, 41.63) * mm});
            skLineSegment(sketch, "E489", {"start": v(-13.48, 41.63) * mm, "end": v(-10.95, 41.99) * mm});
            skLineSegment(sketch, "E490", {"start": v(-15.5, 44.7) * mm, "end": v(-12.08, 44.29) * mm});
            skLineSegment(sketch, "E491", {"start": v(-12.08, 44.29) * mm, "end": v(-10.95, 41.99) * mm});
            skLineSegment(sketch, "E492", {"start": v(-11.94, 48.97) * mm, "end": v(-12.38, 46.45) * mm});
            skLineSegment(sketch, "E493", {"start": v(-12.38, 46.45) * mm, "end": v(-15.56, 45.1) * mm});
            skLineSegment(sketch, "E494", {"start": v(-15.93, 45.48) * mm, "end": v(-14.47, 48.6) * mm});
            skLineSegment(sketch, "E495", {"start": v(-14.47, 48.6) * mm, "end": v(-11.94, 48.97) * mm});
            skArc(sketch, "E496", {"start": v(-16.9, 44.43) * mm, "mid": v(-16.79, 44.28) * mm, "end": v(-16.63, 44.15) * mm});
            skArc(sketch, "E497.trimOffspring", {"start": v(-16.8, 45.3) * mm, "mid": v(-16.91, 45.15) * mm, "end": v(-16.98, 44.96) * mm});
            skArc(sketch, "E498.trimOffspring", {"start": v(-15.93, 45.48) * mm, "mid": v(-16.12, 45.54) * mm, "end": v(-16.32, 45.54) * mm});
            skArc(sketch, "E499.trimOffspring", {"start": v(-15.5, 44.7) * mm, "mid": v(-15.5, 44.9) * mm, "end": v(-15.56, 45.1) * mm});
            skArc(sketch, "E500.trimOffspring", {"start": v(-16.1, 44.06) * mm, "mid": v(-15.92, 44.12) * mm, "end": v(-15.75, 44.23) * mm});
            skLineSegment(sketch, "E501", {"start": v(-18.28, 48.95) * mm, "end": v(-18.42, 48.1) * mm});
            skLineSegment(sketch, "E502", {"start": v(-18.42, 48.1) * mm, "end": v(-17.4, 47.15) * mm});
            skLineSegment(sketch, "E503", {"start": v(-17.4, 47.15) * mm, "end": v(-17.53, 48.54) * mm});
            skLineSegment(sketch, "E504", {"start": v(-17.53, 48.54) * mm, "end": v(-18.28, 48.95) * mm});
            skLineSegment(sketch, "E505", {"start": v(-12.93, 48.01) * mm, "end": v(-13.08, 47.17) * mm});
            skLineSegment(sketch, "E506", {"start": v(-13.08, 47.17) * mm, "end": v(-14.37, 46.62) * mm});
            skLineSegment(sketch, "E507", {"start": v(-14.37, 46.62) * mm, "end": v(-13.78, 47.89) * mm});
            skLineSegment(sketch, "E508", {"start": v(-13.78, 47.89) * mm, "end": v(-12.93, 48.01) * mm});
            skLineSegment(sketch, "E509", {"start": v(-17.04, 40.25) * mm, "end": v(-16.43, 40.84) * mm});
            skLineSegment(sketch, "E510", {"start": v(-16.43, 40.84) * mm, "end": v(-16.7, 42.22) * mm});
            skLineSegment(sketch, "E511", {"start": v(-16.7, 42.22) * mm, "end": v(-17.42, 41.02) * mm});
            skLineSegment(sketch, "E512", {"start": v(-17.42, 41.02) * mm, "end": v(-17.04, 40.25) * mm});
            skLineSegment(sketch, "E513", {"start": v(-12.17, 42.64) * mm, "end": v(-12.54, 43.4) * mm});
            skLineSegment(sketch, "E514", {"start": v(-12.54, 43.4) * mm, "end": v(-13.94, 43.57) * mm});
            skLineSegment(sketch, "E515", {"start": v(-13.94, 43.57) * mm, "end": v(-13.01, 42.52) * mm});
            skLineSegment(sketch, "E516", {"start": v(-13.01, 42.52) * mm, "end": v(-12.17, 42.64) * mm});
            skLineSegment(sketch, "E517", {"start": v(-20.82, 44.15) * mm, "end": v(-20.07, 43.75) * mm});
            skLineSegment(sketch, "E518", {"start": v(-20.07, 43.75) * mm, "end": v(-18.84, 44.43) * mm});
            skLineSegment(sketch, "E519", {"start": v(-18.84, 44.43) * mm, "end": v(-20.2, 44.74) * mm});
            skLineSegment(sketch, "E520", {"start": v(-20.2, 44.74) * mm, "end": v(-20.82, 44.15) * mm});
            skLineSegment(sketch, "E521", {"start": v(-16.71, -47.2) * mm, "end": v(-15.43, -49.41) * mm});
            skLineSegment(sketch, "E522", {"start": v(-15.43, -49.41) * mm, "end": v(-11.98, -49.6) * mm});
            skLineSegment(sketch, "E523", {"start": v(-11.76, -49.1) * mm, "end": v(-14.2, -46.67) * mm});
            skLineSegment(sketch, "E524", {"start": v(-14.2, -46.67) * mm, "end": v(-16.71, -47.2) * mm});
            skLineSegment(sketch, "E525", {"start": v(-15.23, -54.1) * mm, "end": v(-12.73, -53.56) * mm});
            skLineSegment(sketch, "E526", {"start": v(-12.73, -53.56) * mm, "end": v(-11.5, -50.33) * mm});
            skLineSegment(sketch, "E527", {"start": v(-11.9, -49.98) * mm, "end": v(-14.97, -51.56) * mm});
            skLineSegment(sketch, "E528", {"start": v(-14.97, -51.56) * mm, "end": v(-15.23, -54.1) * mm});
            skLineSegment(sketch, "E529", {"start": v(-8.22, -54.83) * mm, "end": v(-7.96, -52.28) * mm});
            skLineSegment(sketch, "E530", {"start": v(-7.96, -52.28) * mm, "end": v(-10.64, -50.1) * mm});
            skLineSegment(sketch, "E531", {"start": v(-11.1, -50.37) * mm, "end": v(-10.56, -53.78) * mm});
            skLineSegment(sketch, "E532", {"start": v(-10.56, -53.78) * mm, "end": v(-8.22, -54.83) * mm});
            skLineSegment(sketch, "E533", {"start": v(-10.49, -49.75) * mm, "end": v(-7.07, -50.28) * mm});
            skLineSegment(sketch, "E534", {"start": v(-7.07, -50.28) * mm, "end": v(-5.36, -48.38) * mm});
            skLineSegment(sketch, "E535", {"start": v(-10.6, -49.23) * mm, "end": v(-7.7, -47.34) * mm});
            skLineSegment(sketch, "E536", {"start": v(-7.7, -47.34) * mm, "end": v(-5.36, -48.38) * mm});
            skLineSegment(sketch, "E537", {"start": v(-10.61, -43.67) * mm, "end": v(-9.33, -45.88) * mm});
            skLineSegment(sketch, "E538", {"start": v(-9.33, -45.88) * mm, "end": v(-10.89, -48.97) * mm});
            skLineSegment(sketch, "E539", {"start": v(-11.42, -48.91) * mm, "end": v(-12.32, -45.57) * mm});
            skLineSegment(sketch, "E540", {"start": v(-12.32, -45.57) * mm, "end": v(-10.61, -43.67) * mm});
            skArc(sketch, "E541", {"start": v(-11.5, -50.33) * mm, "mid": v(-11.3, -50.38) * mm, "end": v(-11.1, -50.37) * mm});
            skArc(sketch, "E542.trimOffspring", {"start": v(-11.98, -49.6) * mm, "mid": v(-11.96, -49.8) * mm, "end": v(-11.9, -49.98) * mm});
            skArc(sketch, "E543.trimOffspring", {"start": v(-11.42, -48.91) * mm, "mid": v(-11.6, -48.99) * mm, "end": v(-11.76, -49.1) * mm});
            skArc(sketch, "E544.trimOffspring", {"start": v(-10.6, -49.23) * mm, "mid": v(-10.73, -49.08) * mm, "end": v(-10.89, -48.97) * mm});
            skArc(sketch, "E545.trimOffspring", {"start": v(-10.64, -50.1) * mm, "mid": v(-10.54, -49.94) * mm, "end": v(-10.49, -49.75) * mm});
            skLineSegment(sketch, "E546", {"start": v(-15.45, -47.76) * mm, "end": v(-15.02, -48.5) * mm});
            skLineSegment(sketch, "E547", {"start": v(-15.02, -48.5) * mm, "end": v(-13.62, -48.57) * mm});
            skLineSegment(sketch, "E548", {"start": v(-13.62, -48.57) * mm, "end": v(-14.62, -47.59) * mm});
            skLineSegment(sketch, "E549", {"start": v(-14.62, -47.59) * mm, "end": v(-15.45, -47.76) * mm});
            skLineSegment(sketch, "E550", {"start": v(-10.75, -45.04) * mm, "end": v(-10.33, -45.78) * mm});
            skLineSegment(sketch, "E551", {"start": v(-10.33, -45.78) * mm, "end": v(-10.96, -47.03) * mm});
            skLineSegment(sketch, "E552", {"start": v(-10.96, -47.03) * mm, "end": v(-11.32, -45.68) * mm});
            skLineSegment(sketch, "E553", {"start": v(-11.32, -45.68) * mm, "end": v(-10.75, -45.04) * mm});
            skLineSegment(sketch, "E554", {"start": v(-8.91, -53.63) * mm, "end": v(-8.83, -52.78) * mm});
            skLineSegment(sketch, "E555", {"start": v(-8.83, -52.78) * mm, "end": v(-9.91, -51.9) * mm});
            skLineSegment(sketch, "E556", {"start": v(-9.91, -51.9) * mm, "end": v(-9.7, -53.28) * mm});
            skLineSegment(sketch, "E557", {"start": v(-9.7, -53.28) * mm, "end": v(-8.91, -53.63) * mm});
            skLineSegment(sketch, "E558", {"start": v(-6.71, -48.67) * mm, "end": v(-7.5, -48.32) * mm});
            skLineSegment(sketch, "E559", {"start": v(-7.5, -48.32) * mm, "end": v(-8.67, -49.09) * mm});
            skLineSegment(sketch, "E560", {"start": v(-8.67, -49.09) * mm, "end": v(-7.28, -49.3) * mm});
            skLineSegment(sketch, "E561", {"start": v(-7.28, -49.3) * mm, "end": v(-6.71, -48.67) * mm});
            skLineSegment(sketch, "E562", {"start": v(-14.31, -53.07) * mm, "end": v(-13.48, -52.9) * mm});
            skLineSegment(sketch, "E563", {"start": v(-13.48, -52.9) * mm, "end": v(-12.98, -51.58) * mm});
            skLineSegment(sketch, "E564", {"start": v(-12.98, -51.58) * mm, "end": v(-14.22, -52.22) * mm});
            skLineSegment(sketch, "E565", {"start": v(-14.22, -52.22) * mm, "end": v(-14.31, -53.07) * mm});
            skLineSegment(sketch, "E566", {"start": v(-52.05, 48.83) * mm, "end": v(-52.04, 46.27) * mm});
            skLineSegment(sketch, "E567", {"start": v(-52.04, 46.27) * mm, "end": v(-49.15, 44.39) * mm});
            skLineSegment(sketch, "E568", {"start": v(-48.71, 44.7) * mm, "end": v(-49.62, 48.03) * mm});
            skLineSegment(sketch, "E569", {"start": v(-49.62, 48.03) * mm, "end": v(-52.05, 48.83) * mm});
            skLineSegment(sketch, "E570", {"start": v(-54.22, 42.11) * mm, "end": v(-51.78, 41.33) * mm});
            skLineSegment(sketch, "E571", {"start": v(-51.78, 41.33) * mm, "end": v(-49.1, 43.5) * mm});
            skLineSegment(sketch, "E572", {"start": v(-49.27, 44.01) * mm, "end": v(-52.72, 44.18) * mm});
            skLineSegment(sketch, "E573", {"start": v(-52.72, 44.18) * mm, "end": v(-54.22, 42.11) * mm});
            skLineSegment(sketch, "E574", {"start": v(-48.5, 37.98) * mm, "end": v(-47.01, 40.05) * mm});
            skLineSegment(sketch, "E575", {"start": v(-47.01, 40.05) * mm, "end": v(-48.25, 43.28) * mm});
            skLineSegment(sketch, "E576", {"start": v(-48.78, 43.28) * mm, "end": v(-50.01, 40.05) * mm});
            skLineSegment(sketch, "E577", {"start": v(-50.01, 40.05) * mm, "end": v(-48.5, 37.98) * mm});
            skLineSegment(sketch, "E578", {"start": v(-47.93, 43.5) * mm, "end": v(-45.24, 41.34) * mm});
            skLineSegment(sketch, "E579", {"start": v(-45.24, 41.34) * mm, "end": v(-42.8, 42.13) * mm});
            skLineSegment(sketch, "E580", {"start": v(-47.77, 44.02) * mm, "end": v(-44.32, 44.2) * mm});
            skLineSegment(sketch, "E581", {"start": v(-44.32, 44.2) * mm, "end": v(-42.8, 42.13) * mm});
            skLineSegment(sketch, "E582", {"start": v(-45, 48.84) * mm, "end": v(-45, 46.28) * mm});
            skLineSegment(sketch, "E583", {"start": v(-45, 46.28) * mm, "end": v(-47.9, 44.39) * mm});
            skLineSegment(sketch, "E584", {"start": v(-48.32, 44.7) * mm, "end": v(-47.43, 48.04) * mm});
            skLineSegment(sketch, "E585", {"start": v(-47.43, 48.04) * mm, "end": v(-45, 48.84) * mm});
            skArc(sketch, "E586", {"start": v(-49.1, 43.5) * mm, "mid": v(-48.96, 43.37) * mm, "end": v(-48.78, 43.28) * mm});
            skArc(sketch, "E587.trimOffspring", {"start": v(-49.15, 44.39) * mm, "mid": v(-49.23, 44.2) * mm, "end": v(-49.27, 44.01) * mm});
            skArc(sketch, "E588.trimOffspring", {"start": v(-48.32, 44.7) * mm, "mid": v(-48.52, 44.73) * mm, "end": v(-48.71, 44.7) * mm});
            skArc(sketch, "E589.trimOffspring", {"start": v(-47.77, 44.02) * mm, "mid": v(-47.8, 44.21) * mm, "end": v(-47.9, 44.39) * mm});
            skArc(sketch, "E590.trimOffspring", {"start": v(-48.25, 43.28) * mm, "mid": v(-48.08, 43.37) * mm, "end": v(-47.93, 43.5) * mm});
            skLineSegment(sketch, "E591", {"start": v(-51.24, 47.7) * mm, "end": v(-51.24, 46.86) * mm});
            skLineSegment(sketch, "E592", {"start": v(-51.24, 46.86) * mm, "end": v(-50.06, 46.1) * mm});
            skLineSegment(sketch, "E593", {"start": v(-50.06, 46.1) * mm, "end": v(-50.43, 47.45) * mm});
            skLineSegment(sketch, "E594", {"start": v(-50.43, 47.45) * mm, "end": v(-51.24, 47.7) * mm});
            skLineSegment(sketch, "E595", {"start": v(-45.8, 47.72) * mm, "end": v(-45.8, 46.87) * mm});
            skLineSegment(sketch, "E596", {"start": v(-45.8, 46.87) * mm, "end": v(-46.98, 46.1) * mm});
            skLineSegment(sketch, "E597", {"start": v(-46.98, 46.1) * mm, "end": v(-46.62, 47.45) * mm});
            skLineSegment(sketch, "E598", {"start": v(-46.62, 47.45) * mm, "end": v(-45.8, 47.72) * mm});
            skLineSegment(sketch, "E599", {"start": v(-48.51, 39.36) * mm, "end": v(-48.01, 40.05) * mm});
            skLineSegment(sketch, "E600", {"start": v(-48.01, 40.05) * mm, "end": v(-48.51, 41.36) * mm});
            skLineSegment(sketch, "E601", {"start": v(-48.51, 41.36) * mm, "end": v(-49.01, 40.05) * mm});
            skLineSegment(sketch, "E602", {"start": v(-49.01, 40.05) * mm, "end": v(-48.51, 39.36) * mm});
            skLineSegment(sketch, "E603", {"start": v(-44.12, 42.56) * mm, "end": v(-44.63, 43.25) * mm});
            skLineSegment(sketch, "E604", {"start": v(-44.63, 43.25) * mm, "end": v(-46.03, 43.17) * mm});
            skLineSegment(sketch, "E605", {"start": v(-46.03, 43.17) * mm, "end": v(-44.93, 42.3) * mm});
            skLineSegment(sketch, "E606", {"start": v(-44.93, 42.3) * mm, "end": v(-44.12, 42.56) * mm});
            skLineSegment(sketch, "E607", {"start": v(-52.9, 42.54) * mm, "end": v(-52.1, 42.28) * mm});
            skLineSegment(sketch, "E608", {"start": v(-52.1, 42.28) * mm, "end": v(-51, 43.16) * mm});
            skLineSegment(sketch, "E609", {"start": v(-51, 43.16) * mm, "end": v(-52.4, 43.23) * mm});
            skLineSegment(sketch, "E610", {"start": v(-52.4, 43.23) * mm, "end": v(-52.9, 42.54) * mm});
            skLineSegment(sketch, "E611", {"start": v(-63.31, 52.53) * mm, "end": v(-65.63, 51.44) * mm});
            skLineSegment(sketch, "E612", {"start": v(-65.63, 51.44) * mm, "end": v(-66.1, 48.02) * mm});
            skLineSegment(sketch, "E613", {"start": v(-65.64, 47.76) * mm, "end": v(-63, 50) * mm});
            skLineSegment(sketch, "E614", {"start": v(-63, 50) * mm, "end": v(-63.31, 52.53) * mm});
            skLineSegment(sketch, "E615", {"start": v(-70.31, 51.66) * mm, "end": v(-70, 49.12) * mm});
            skLineSegment(sketch, "E616", {"start": v(-70, 49.12) * mm, "end": v(-66.89, 47.6) * mm});
            skLineSegment(sketch, "E617", {"start": v(-66.5, 47.97) * mm, "end": v(-67.8, 51.17) * mm});
            skLineSegment(sketch, "E618", {"start": v(-67.8, 51.17) * mm, "end": v(-70.31, 51.66) * mm});
            skLineSegment(sketch, "E619", {"start": v(-71.65, 44.73) * mm, "end": v(-69.13, 44.25) * mm});
            skLineSegment(sketch, "E620", {"start": v(-69.13, 44.25) * mm, "end": v(-66.73, 46.74) * mm});
            skLineSegment(sketch, "E621", {"start": v(-66.96, 47.22) * mm, "end": v(-70.4, 46.97) * mm});
            skLineSegment(sketch, "E622", {"start": v(-70.4, 46.97) * mm, "end": v(-71.65, 44.73) * mm});
            skLineSegment(sketch, "E623", {"start": v(-66.4, 46.55) * mm, "end": v(-67.22, 43.2) * mm});
            skLineSegment(sketch, "E624", {"start": v(-67.22, 43.2) * mm, "end": v(-65.47, 41.32) * mm});
            skLineSegment(sketch, "E625", {"start": v(-65.86, 46.62) * mm, "end": v(-64.24, 43.57) * mm});
            skLineSegment(sketch, "E626", {"start": v(-64.24, 43.57) * mm, "end": v(-65.47, 41.32) * mm});
            skLineSegment(sketch, "E627", {"start": v(-60.32, 46.14) * mm, "end": v(-62.64, 45.06) * mm});
            skLineSegment(sketch, "E628", {"start": v(-62.64, 45.06) * mm, "end": v(-65.57, 46.88) * mm});
            skLineSegment(sketch, "E629", {"start": v(-65.47, 47.4) * mm, "end": v(-62.07, 48) * mm});
            skLineSegment(sketch, "E630", {"start": v(-62.07, 48) * mm, "end": v(-60.32, 46.14) * mm});
            skArc(sketch, "E631", {"start": v(-66.89, 47.6) * mm, "mid": v(-66.95, 47.42) * mm, "end": v(-66.96, 47.22) * mm});
            skArc(sketch, "E632.trimOffspring", {"start": v(-66.1, 48.02) * mm, "mid": v(-66.3, 48.02) * mm, "end": v(-66.5, 47.97) * mm});
            skArc(sketch, "E633.trimOffspring", {"start": v(-65.47, 47.4) * mm, "mid": v(-65.53, 47.6) * mm, "end": v(-65.64, 47.76) * mm});
            skArc(sketch, "E634.trimOffspring", {"start": v(-65.86, 46.62) * mm, "mid": v(-65.7, 46.73) * mm, "end": v(-65.57, 46.88) * mm});
            skArc(sketch, "E635.trimOffspring", {"start": v(-66.73, 46.74) * mm, "mid": v(-66.57, 46.62) * mm, "end": v(-66.4, 46.55) * mm});
            skLineSegment(sketch, "E636", {"start": v(-63.98, 51.32) * mm, "end": v(-64.75, 50.96) * mm});
            skLineSegment(sketch, "E637", {"start": v(-64.75, 50.96) * mm, "end": v(-64.95, 49.57) * mm});
            skLineSegment(sketch, "E638", {"start": v(-64.95, 49.57) * mm, "end": v(-63.88, 50.47) * mm});
            skLineSegment(sketch, "E639", {"start": v(-63.88, 50.47) * mm, "end": v(-63.98, 51.32) * mm});
            skLineSegment(sketch, "E640", {"start": v(-61.68, 46.4) * mm, "end": v(-62.45, 46.04) * mm});
            skLineSegment(sketch, "E641", {"start": v(-62.45, 46.04) * mm, "end": v(-63.64, 46.78) * mm});
            skLineSegment(sketch, "E642", {"start": v(-63.64, 46.78) * mm, "end": v(-62.26, 47.03) * mm});
            skLineSegment(sketch, "E643", {"start": v(-62.26, 47.03) * mm, "end": v(-61.68, 46.4) * mm});
            skLineSegment(sketch, "E644", {"start": v(-70.4, 45.32) * mm, "end": v(-69.56, 45.16) * mm});
            skLineSegment(sketch, "E645", {"start": v(-69.56, 45.16) * mm, "end": v(-68.58, 46.17) * mm});
            skLineSegment(sketch, "E646", {"start": v(-68.58, 46.17) * mm, "end": v(-69.98, 46.06) * mm});
            skLineSegment(sketch, "E647", {"start": v(-69.98, 46.06) * mm, "end": v(-70.4, 45.32) * mm});
            skLineSegment(sketch, "E648", {"start": v(-65.64, 42.7) * mm, "end": v(-65.23, 43.44) * mm});
            skLineSegment(sketch, "E649", {"start": v(-65.23, 43.44) * mm, "end": v(-65.89, 44.68) * mm});
            skLineSegment(sketch, "E650", {"start": v(-65.89, 44.68) * mm, "end": v(-66.22, 43.32) * mm});
            skLineSegment(sketch, "E651", {"start": v(-66.22, 43.32) * mm, "end": v(-65.64, 42.7) * mm});
            skLineSegment(sketch, "E652", {"start": v(-69.37, 50.65) * mm, "end": v(-69.26, 49.8) * mm});
            skLineSegment(sketch, "E653", {"start": v(-69.26, 49.8) * mm, "end": v(-68, 49.19) * mm});
            skLineSegment(sketch, "E654", {"start": v(-68, 49.19) * mm, "end": v(-68.53, 50.49) * mm});
            skLineSegment(sketch, "E655", {"start": v(-68.53, 50.49) * mm, "end": v(-69.37, 50.65) * mm});
            skLineSegment(sketch, "E656", {"start": v(-36.81, 51.54) * mm, "end": v(-36.14, 49.07) * mm});
            skLineSegment(sketch, "E657", {"start": v(-36.14, 49.07) * mm, "end": v(-32.86, 48) * mm});
            skLineSegment(sketch, "E658", {"start": v(-32.52, 48.42) * mm, "end": v(-34.26, 51.4) * mm});
            skLineSegment(sketch, "E659", {"start": v(-34.26, 51.4) * mm, "end": v(-36.81, 51.54) * mm});
            skLineSegment(sketch, "E660", {"start": v(-37.17, 44.5) * mm, "end": v(-34.62, 44.37) * mm});
            skLineSegment(sketch, "E661", {"start": v(-34.62, 44.37) * mm, "end": v(-32.59, 47.16) * mm});
            skLineSegment(sketch, "E662", {"start": v(-32.88, 47.6) * mm, "end": v(-36.25, 46.88) * mm});
            skLineSegment(sketch, "E663", {"start": v(-36.25, 46.88) * mm, "end": v(-37.17, 44.5) * mm});
            skLineSegment(sketch, "E664", {"start": v(-30.58, 41.97) * mm, "end": v(-29.67, 44.37) * mm});
            skLineSegment(sketch, "E665", {"start": v(-29.67, 44.37) * mm, "end": v(-31.7, 47.16) * mm});
            skLineSegment(sketch, "E666", {"start": v(-32.22, 47.02) * mm, "end": v(-32.57, 43.59) * mm});
            skLineSegment(sketch, "E667", {"start": v(-32.57, 43.59) * mm, "end": v(-30.58, 41.97) * mm});
            skLineSegment(sketch, "E668", {"start": v(-31.46, 47.46) * mm, "end": v(-28.3, 46.07) * mm});
            skLineSegment(sketch, "E669", {"start": v(-28.3, 46.07) * mm, "end": v(-26.15, 47.46) * mm});
            skLineSegment(sketch, "E670", {"start": v(-31.43, 48) * mm, "end": v(-28.15, 49.07) * mm});
            skLineSegment(sketch, "E671", {"start": v(-28.15, 49.07) * mm, "end": v(-26.15, 47.46) * mm});
            skLineSegment(sketch, "E672", {"start": v(-30, 53.37) * mm, "end": v(-29.34, 50.9) * mm});
            skLineSegment(sketch, "E673", {"start": v(-29.34, 50.9) * mm, "end": v(-31.64, 48.33) * mm});
            skLineSegment(sketch, "E674", {"start": v(-32.14, 48.52) * mm, "end": v(-32.14, 51.97) * mm});
            skLineSegment(sketch, "E675", {"start": v(-32.14, 51.97) * mm, "end": v(-30, 53.37) * mm});
            skArc(sketch, "E676", {"start": v(-32.59, 47.16) * mm, "mid": v(-32.41, 47.07) * mm, "end": v(-32.22, 47.02) * mm});
            skArc(sketch, "E677.trimOffspring", {"start": v(-32.86, 48) * mm, "mid": v(-32.9, 47.8) * mm, "end": v(-32.88, 47.6) * mm});
            skArc(sketch, "E678.trimOffspring", {"start": v(-32.14, 48.52) * mm, "mid": v(-32.34, 48.5) * mm, "end": v(-32.52, 48.42) * mm});
            skArc(sketch, "E679.trimOffspring", {"start": v(-31.43, 48) * mm, "mid": v(-31.52, 48.18) * mm, "end": v(-31.64, 48.33) * mm});
            skArc(sketch, "E680.trimOffspring", {"start": v(-31.7, 47.16) * mm, "mid": v(-31.56, 47.3) * mm, "end": v(-31.46, 47.46) * mm});
            skLineSegment(sketch, "E681", {"start": v(-35.74, 50.67) * mm, "end": v(-35.51, 49.84) * mm});
            skLineSegment(sketch, "E682", {"start": v(-35.51, 49.84) * mm, "end": v(-34.18, 49.41) * mm});
            skLineSegment(sketch, "E683", {"start": v(-34.18, 49.41) * mm, "end": v(-34.89, 50.62) * mm});
            skLineSegment(sketch, "E684", {"start": v(-34.89, 50.62) * mm, "end": v(-35.74, 50.67) * mm});
            skLineSegment(sketch, "E685", {"start": v(-30.5, 52.08) * mm, "end": v(-30.28, 51.26) * mm});
            skLineSegment(sketch, "E686", {"start": v(-30.28, 51.26) * mm, "end": v(-31.21, 50.21) * mm});
            skLineSegment(sketch, "E687", {"start": v(-31.21, 50.21) * mm, "end": v(-31.21, 51.61) * mm});
            skLineSegment(sketch, "E688", {"start": v(-31.21, 51.61) * mm, "end": v(-30.5, 52.08) * mm});
            skLineSegment(sketch, "E689", {"start": v(-30.94, 43.3) * mm, "end": v(-30.64, 44.1) * mm});
            skLineSegment(sketch, "E690", {"start": v(-30.64, 44.1) * mm, "end": v(-31.46, 45.24) * mm});
            skLineSegment(sketch, "E691", {"start": v(-31.46, 45.24) * mm, "end": v(-31.6, 43.85) * mm});
            skLineSegment(sketch, "E692", {"start": v(-31.6, 43.85) * mm, "end": v(-30.94, 43.3) * mm});
            skLineSegment(sketch, "E693", {"start": v(-27.53, 47.53) * mm, "end": v(-28.2, 48.07) * mm});
            skLineSegment(sketch, "E694", {"start": v(-28.2, 48.07) * mm, "end": v(-29.53, 47.64) * mm});
            skLineSegment(sketch, "E695", {"start": v(-29.53, 47.64) * mm, "end": v(-28.25, 47.07) * mm});
            skLineSegment(sketch, "E696", {"start": v(-28.25, 47.07) * mm, "end": v(-27.53, 47.53) * mm});
            skLineSegment(sketch, "E697", {"start": v(-36.01, 45.25) * mm, "end": v(-35.16, 45.2) * mm});
            skLineSegment(sketch, "E698", {"start": v(-35.16, 45.2) * mm, "end": v(-34.34, 46.34) * mm});
            skLineSegment(sketch, "E699", {"start": v(-34.34, 46.34) * mm, "end": v(-35.7, 46.04) * mm});
            skLineSegment(sketch, "E700", {"start": v(-35.7, 46.04) * mm, "end": v(-36.01, 45.25) * mm});
            skLineSegment(sketch, "E701", {"start": v(-58.07, -46.27) * mm, "end": v(-55.55, -46.7) * mm});
            skLineSegment(sketch, "E702", {"start": v(-55.55, -46.7) * mm, "end": v(-53.19, -44.18) * mm});
            skLineSegment(sketch, "E703", {"start": v(-53.43, -43.7) * mm, "end": v(-56.86, -44.01) * mm});
            skLineSegment(sketch, "E704", {"start": v(-56.86, -44.01) * mm, "end": v(-58.07, -46.27) * mm});
            skLineSegment(sketch, "E705", {"start": v(-51.83, -49.57) * mm, "end": v(-50.64, -47.3) * mm});
            skLineSegment(sketch, "E706", {"start": v(-50.64, -47.3) * mm, "end": v(-52.31, -44.29) * mm});
            skLineSegment(sketch, "E707", {"start": v(-52.84, -44.36) * mm, "end": v(-53.61, -47.73) * mm});
            skLineSegment(sketch, "E708", {"start": v(-53.61, -47.73) * mm, "end": v(-51.83, -49.57) * mm});
            skLineSegment(sketch, "E709", {"start": v(-46.77, -44.66) * mm, "end": v(-48.55, -42.83) * mm});
            skLineSegment(sketch, "E710", {"start": v(-48.55, -42.83) * mm, "end": v(-51.94, -43.49) * mm});
            skLineSegment(sketch, "E711", {"start": v(-52.03, -44.02) * mm, "end": v(-49.07, -45.78) * mm});
            skLineSegment(sketch, "E712", {"start": v(-49.07, -45.78) * mm, "end": v(-46.77, -44.66) * mm});
            skLineSegment(sketch, "E713", {"start": v(-52.11, -43.14) * mm, "end": v(-49.51, -40.86) * mm});
            skLineSegment(sketch, "E714", {"start": v(-49.51, -40.86) * mm, "end": v(-49.87, -38.33) * mm});
            skLineSegment(sketch, "E715", {"start": v(-52.59, -42.89) * mm, "end": v(-52.17, -39.46) * mm});
            skLineSegment(sketch, "E716", {"start": v(-52.17, -39.46) * mm, "end": v(-49.87, -38.33) * mm});
            skLineSegment(sketch, "E717", {"start": v(-56.85, -39.32) * mm, "end": v(-54.33, -39.77) * mm});
            skLineSegment(sketch, "E718", {"start": v(-54.33, -39.77) * mm, "end": v(-52.97, -42.94) * mm});
            skLineSegment(sketch, "E719", {"start": v(-53.36, -43.31) * mm, "end": v(-56.49, -41.86) * mm});
            skLineSegment(sketch, "E720", {"start": v(-56.49, -41.86) * mm, "end": v(-56.85, -39.32) * mm});
            skArc(sketch, "E721", {"start": v(-52.31, -44.29) * mm, "mid": v(-52.16, -44.17) * mm, "end": v(-52.03, -44.02) * mm});
            skArc(sketch, "E722.trimOffspring", {"start": v(-53.19, -44.18) * mm, "mid": v(-53.03, -44.3) * mm, "end": v(-52.84, -44.36) * mm});
            skArc(sketch, "E723.trimOffspring", {"start": v(-53.36, -43.31) * mm, "mid": v(-53.42, -43.5) * mm, "end": v(-53.43, -43.7) * mm});
            skArc(sketch, "E724.trimOffspring", {"start": v(-52.59, -42.89) * mm, "mid": v(-52.78, -42.89) * mm, "end": v(-52.97, -42.94) * mm});
            skArc(sketch, "E725.trimOffspring", {"start": v(-51.94, -43.49) * mm, "mid": v(-52, -43.3) * mm, "end": v(-52.11, -43.14) * mm});
            skLineSegment(sketch, "E726", {"start": v(-56.83, -45.66) * mm, "end": v(-55.99, -45.8) * mm});
            skLineSegment(sketch, "E727", {"start": v(-55.99, -45.8) * mm, "end": v(-55.03, -44.78) * mm});
            skLineSegment(sketch, "E728", {"start": v(-55.03, -44.78) * mm, "end": v(-56.43, -44.91) * mm});
            skLineSegment(sketch, "E729", {"start": v(-56.43, -44.91) * mm, "end": v(-56.83, -45.66) * mm});
            skLineSegment(sketch, "E730", {"start": v(-55.9, -40.32) * mm, "end": v(-55.05, -40.46) * mm});
            skLineSegment(sketch, "E731", {"start": v(-55.05, -40.46) * mm, "end": v(-54.5, -41.75) * mm});
            skLineSegment(sketch, "E732", {"start": v(-54.5, -41.75) * mm, "end": v(-55.77, -41.16) * mm});
            skLineSegment(sketch, "E733", {"start": v(-55.77, -41.16) * mm, "end": v(-55.9, -40.32) * mm});
            skLineSegment(sketch, "E734", {"start": v(-48.13, -44.43) * mm, "end": v(-48.72, -43.81) * mm});
            skLineSegment(sketch, "E735", {"start": v(-48.72, -43.81) * mm, "end": v(-50.1, -44.08) * mm});
            skLineSegment(sketch, "E736", {"start": v(-50.1, -44.08) * mm, "end": v(-48.9, -44.8) * mm});
            skLineSegment(sketch, "E737", {"start": v(-48.9, -44.8) * mm, "end": v(-48.13, -44.43) * mm});
            skLineSegment(sketch, "E738", {"start": v(-50.52, -39.55) * mm, "end": v(-51.28, -39.93) * mm});
            skLineSegment(sketch, "E739", {"start": v(-51.28, -39.93) * mm, "end": v(-51.45, -41.32) * mm});
            skLineSegment(sketch, "E740", {"start": v(-51.45, -41.32) * mm, "end": v(-50.4, -40.4) * mm});
            skLineSegment(sketch, "E741", {"start": v(-50.4, -40.4) * mm, "end": v(-50.52, -39.55) * mm});
            skLineSegment(sketch, "E742", {"start": v(-52.03, -48.2) * mm, "end": v(-51.63, -47.45) * mm});
            skLineSegment(sketch, "E743", {"start": v(-51.63, -47.45) * mm, "end": v(-52.3, -46.22) * mm});
            skLineSegment(sketch, "E744", {"start": v(-52.3, -46.22) * mm, "end": v(-52.62, -47.6) * mm});
            skLineSegment(sketch, "E745", {"start": v(-52.62, -47.6) * mm, "end": v(-52.03, -48.2) * mm});
            skLineSegment(sketch, "E746", {"start": v(38.15, -42.12) * mm, "end": v(40.12, -43.76) * mm});
            skLineSegment(sketch, "E747", {"start": v(40.12, -43.76) * mm, "end": v(43.42, -42.75) * mm});
            skLineSegment(sketch, "E748", {"start": v(43.46, -42.21) * mm, "end": v(40.32, -40.76) * mm});
            skLineSegment(sketch, "E749", {"start": v(40.32, -40.76) * mm, "end": v(38.15, -42.12) * mm});
            skLineSegment(sketch, "E750", {"start": v(41.9, -48.1) * mm, "end": v(44.07, -46.73) * mm});
            skLineSegment(sketch, "E751", {"start": v(44.07, -46.73) * mm, "end": v(44.13, -43.28) * mm});
            skLineSegment(sketch, "E752", {"start": v(43.63, -43.08) * mm, "end": v(41.28, -45.61) * mm});
            skLineSegment(sketch, "E753", {"start": v(41.28, -45.61) * mm, "end": v(41.9, -48.1) * mm});
            skLineSegment(sketch, "E754", {"start": v(48.74, -46.38) * mm, "end": v(48.11, -43.9) * mm});
            skLineSegment(sketch, "E755", {"start": v(48.11, -43.9) * mm, "end": v(44.85, -42.77) * mm});
            skLineSegment(sketch, "E756", {"start": v(44.5, -43.18) * mm, "end": v(46.19, -46.2) * mm});
            skLineSegment(sketch, "E757", {"start": v(46.19, -46.2) * mm, "end": v(48.74, -46.38) * mm});
            skLineSegment(sketch, "E758", {"start": v(44.87, -42.38) * mm, "end": v(48.26, -41.71) * mm});
            skLineSegment(sketch, "E759", {"start": v(48.26, -41.71) * mm, "end": v(49.22, -39.34) * mm});
            skLineSegment(sketch, "E760", {"start": v(44.59, -41.93) * mm, "end": v(46.67, -39.17) * mm});
            skLineSegment(sketch, "E761", {"start": v(46.67, -39.17) * mm, "end": v(49.22, -39.34) * mm});
            skLineSegment(sketch, "E762", {"start": v(42.68, -36.7) * mm, "end": v(44.64, -38.35) * mm});
            skLineSegment(sketch, "E763", {"start": v(44.64, -38.35) * mm, "end": v(44.23, -41.78) * mm});
            skLineSegment(sketch, "E764", {"start": v(43.7, -41.91) * mm, "end": v(41.73, -39.08) * mm});
            skLineSegment(sketch, "E765", {"start": v(41.73, -39.08) * mm, "end": v(42.68, -36.7) * mm});
            skArc(sketch, "E766", {"start": v(44.13, -43.28) * mm, "mid": v(44.32, -43.25) * mm, "end": v(44.5, -43.18) * mm});
            skArc(sketch, "E767.trimOffspring", {"start": v(43.42, -42.75) * mm, "mid": v(43.5, -42.93) * mm, "end": v(43.63, -43.08) * mm});
            skArc(sketch, "E768.trimOffspring", {"start": v(43.7, -41.91) * mm, "mid": v(43.56, -42.05) * mm, "end": v(43.46, -42.21) * mm});
            skArc(sketch, "E769.trimOffspring", {"start": v(44.59, -41.93) * mm, "mid": v(44.42, -41.83) * mm, "end": v(44.23, -41.78) * mm});
            skArc(sketch, "E770.trimOffspring", {"start": v(44.85, -42.77) * mm, "mid": v(44.89, -42.58) * mm, "end": v(44.87, -42.38) * mm});
            skLineSegment(sketch, "E771", {"start": v(39.53, -42.21) * mm, "end": v(40.19, -42.76) * mm});
            skLineSegment(sketch, "E772", {"start": v(40.19, -42.76) * mm, "end": v(41.53, -42.35) * mm});
            skLineSegment(sketch, "E773", {"start": v(41.53, -42.35) * mm, "end": v(40.25, -41.76) * mm});
            skLineSegment(sketch, "E774", {"start": v(40.25, -41.76) * mm, "end": v(39.53, -42.21) * mm});
            skLineSegment(sketch, "E775", {"start": v(43.01, -38.05) * mm, "end": v(43.67, -38.6) * mm});
            skLineSegment(sketch, "E776", {"start": v(43.67, -38.6) * mm, "end": v(43.5, -39.99) * mm});
            skLineSegment(sketch, "E777", {"start": v(43.5, -39.99) * mm, "end": v(42.7, -38.84) * mm});
            skLineSegment(sketch, "E778", {"start": v(42.7, -38.84) * mm, "end": v(43.01, -38.05) * mm});
            skLineSegment(sketch, "E779", {"start": v(47.68, -45.49) * mm, "end": v(47.47, -44.66) * mm});
            skLineSegment(sketch, "E780", {"start": v(47.47, -44.66) * mm, "end": v(46.15, -44.2) * mm});
            skLineSegment(sketch, "E781", {"start": v(46.15, -44.2) * mm, "end": v(46.83, -45.43) * mm});
            skLineSegment(sketch, "E782", {"start": v(46.83, -45.43) * mm, "end": v(47.68, -45.49) * mm});
            skLineSegment(sketch, "E783", {"start": v(48.05, -40.07) * mm, "end": v(47.2, -40.02) * mm});
            skLineSegment(sketch, "E784", {"start": v(47.2, -40.02) * mm, "end": v(46.35, -41.14) * mm});
            skLineSegment(sketch, "E785", {"start": v(46.35, -41.14) * mm, "end": v(47.73, -40.86) * mm});
            skLineSegment(sketch, "E786", {"start": v(47.73, -40.86) * mm, "end": v(48.05, -40.07) * mm});
            skLineSegment(sketch, "E787", {"start": v(42.42, -46.81) * mm, "end": v(43.14, -46.36) * mm});
            skLineSegment(sketch, "E788", {"start": v(43.14, -46.36) * mm, "end": v(43.16, -44.96) * mm});
            skLineSegment(sketch, "E789", {"start": v(43.16, -44.96) * mm, "end": v(42.2, -45.98) * mm});
            skLineSegment(sketch, "E790", {"start": v(42.2, -45.98) * mm, "end": v(42.42, -46.81) * mm});
            skLineSegment(sketch, "E791", {"start": v(-38.53, -42.41) * mm, "end": v(-37.86, -44.88) * mm});
            skLineSegment(sketch, "E792", {"start": v(-37.86, -44.88) * mm, "end": v(-34.57, -45.95) * mm});
            skLineSegment(sketch, "E793", {"start": v(-34.23, -45.53) * mm, "end": v(-35.97, -42.55) * mm});
            skLineSegment(sketch, "E794", {"start": v(-35.97, -42.55) * mm, "end": v(-38.53, -42.41) * mm});
            skLineSegment(sketch, "E795", {"start": v(-38.88, -49.46) * mm, "end": v(-36.33, -49.58) * mm});
            skLineSegment(sketch, "E796", {"start": v(-36.33, -49.58) * mm, "end": v(-34.3, -46.79) * mm});
            skLineSegment(sketch, "E797", {"start": v(-34.6, -46.34) * mm, "end": v(-37.97, -47.07) * mm});
            skLineSegment(sketch, "E798", {"start": v(-37.97, -47.07) * mm, "end": v(-38.88, -49.46) * mm});
            skLineSegment(sketch, "E799", {"start": v(-32.3, -51.97) * mm, "end": v(-31.39, -49.58) * mm});
            skLineSegment(sketch, "E800", {"start": v(-31.39, -49.58) * mm, "end": v(-33.42, -46.79) * mm});
            skLineSegment(sketch, "E801", {"start": v(-33.93, -46.93) * mm, "end": v(-34.28, -50.36) * mm});
            skLineSegment(sketch, "E802", {"start": v(-34.28, -50.36) * mm, "end": v(-32.3, -51.97) * mm});
            skLineSegment(sketch, "E803", {"start": v(-33.17, -46.48) * mm, "end": v(-30.01, -47.88) * mm});
            skLineSegment(sketch, "E804", {"start": v(-30.01, -47.88) * mm, "end": v(-27.87, -46.49) * mm});
            skLineSegment(sketch, "E805", {"start": v(-33.14, -45.95) * mm, "end": v(-29.86, -44.88) * mm});
            skLineSegment(sketch, "E806", {"start": v(-29.86, -44.88) * mm, "end": v(-27.87, -46.49) * mm});
            skLineSegment(sketch, "E807", {"start": v(-31.72, -40.58) * mm, "end": v(-31.05, -43.05) * mm});
            skLineSegment(sketch, "E808", {"start": v(-31.05, -43.05) * mm, "end": v(-33.36, -45.62) * mm});
            skLineSegment(sketch, "E809", {"start": v(-33.86, -45.43) * mm, "end": v(-33.86, -41.98) * mm});
            skLineSegment(sketch, "E810", {"start": v(-33.86, -41.98) * mm, "end": v(-31.72, -40.58) * mm});
            skArc(sketch, "E811", {"start": v(-34.3, -46.79) * mm, "mid": v(-34.13, -46.88) * mm, "end": v(-33.93, -46.93) * mm});
            skArc(sketch, "E812.trimOffspring", {"start": v(-34.57, -45.95) * mm, "mid": v(-34.6, -46.14) * mm, "end": v(-34.6, -46.34) * mm});
            skArc(sketch, "E813.trimOffspring", {"start": v(-33.86, -45.43) * mm, "mid": v(-34.05, -45.46) * mm, "end": v(-34.23, -45.53) * mm});
            skArc(sketch, "E814.trimOffspring", {"start": v(-33.14, -45.95) * mm, "mid": v(-33.23, -45.77) * mm, "end": v(-33.36, -45.62) * mm});
            skArc(sketch, "E815.trimOffspring", {"start": v(-33.42, -46.79) * mm, "mid": v(-33.27, -46.65) * mm, "end": v(-33.17, -46.48) * mm});
            skLineSegment(sketch, "E816", {"start": v(-37.45, -43.28) * mm, "end": v(-37.23, -44.1) * mm});
            skLineSegment(sketch, "E817", {"start": v(-37.23, -44.1) * mm, "end": v(-35.9, -44.54) * mm});
            skLineSegment(sketch, "E818", {"start": v(-35.9, -44.54) * mm, "end": v(-36.6, -43.33) * mm});
            skLineSegment(sketch, "E819", {"start": v(-36.6, -43.33) * mm, "end": v(-37.45, -43.28) * mm});
            skLineSegment(sketch, "E820", {"start": v(-32.2, -41.87) * mm, "end": v(-31.99, -42.7) * mm});
            skLineSegment(sketch, "E821", {"start": v(-31.99, -42.7) * mm, "end": v(-32.92, -43.74) * mm});
            skLineSegment(sketch, "E822", {"start": v(-32.92, -43.74) * mm, "end": v(-32.92, -42.33) * mm});
            skLineSegment(sketch, "E823", {"start": v(-32.92, -42.33) * mm, "end": v(-32.2, -41.87) * mm});
            skLineSegment(sketch, "E824", {"start": v(-32.65, -50.64) * mm, "end": v(-32.35, -49.84) * mm});
            skLineSegment(sketch, "E825", {"start": v(-32.35, -49.84) * mm, "end": v(-33.18, -48.7) * mm});
            skLineSegment(sketch, "E826", {"start": v(-33.18, -48.7) * mm, "end": v(-33.32, -50.1) * mm});
            skLineSegment(sketch, "E827", {"start": v(-33.32, -50.1) * mm, "end": v(-32.65, -50.64) * mm});
            skLineSegment(sketch, "E828", {"start": v(-29.24, -46.42) * mm, "end": v(-29.91, -45.88) * mm});
            skLineSegment(sketch, "E829", {"start": v(-29.91, -45.88) * mm, "end": v(-31.24, -46.31) * mm});
            skLineSegment(sketch, "E830", {"start": v(-31.24, -46.31) * mm, "end": v(-29.96, -46.88) * mm});
            skLineSegment(sketch, "E831", {"start": v(-29.96, -46.88) * mm, "end": v(-29.24, -46.42) * mm});
            skLineSegment(sketch, "E832", {"start": v(-37.73, -48.7) * mm, "end": v(-36.87, -48.74) * mm});
            skLineSegment(sketch, "E833", {"start": v(-36.87, -48.74) * mm, "end": v(-36.05, -47.61) * mm});
            skLineSegment(sketch, "E834", {"start": v(-36.05, -47.61) * mm, "end": v(-37.42, -47.9) * mm});
            skLineSegment(sketch, "E835", {"start": v(-37.42, -47.9) * mm, "end": v(-37.73, -48.7) * mm});
            skLineSegment(sketch, "E836", {"start": v(-70.53, -42.21) * mm, "end": v(-70.52, -44.77) * mm});
            skLineSegment(sketch, "E837", {"start": v(-70.52, -44.77) * mm, "end": v(-67.63, -46.65) * mm});
            skLineSegment(sketch, "E838", {"start": v(-67.2, -46.34) * mm, "end": v(-68.1, -43) * mm});
            skLineSegment(sketch, "E839", {"start": v(-68.1, -43) * mm, "end": v(-70.53, -42.21) * mm});
            skLineSegment(sketch, "E840", {"start": v(-72.7, -48.92) * mm, "end": v(-70.26, -49.7) * mm});
            skLineSegment(sketch, "E841", {"start": v(-70.26, -49.7) * mm, "end": v(-67.58, -47.53) * mm});
            skLineSegment(sketch, "E842", {"start": v(-67.75, -47.02) * mm, "end": v(-71.2, -46.85) * mm});
            skLineSegment(sketch, "E843", {"start": v(-71.2, -46.85) * mm, "end": v(-72.7, -48.92) * mm});
            skLineSegment(sketch, "E844", {"start": v(-66.99, -53.06) * mm, "end": v(-65.5, -50.98) * mm});
            skLineSegment(sketch, "E845", {"start": v(-65.5, -50.98) * mm, "end": v(-66.73, -47.76) * mm});
            skLineSegment(sketch, "E846", {"start": v(-67.26, -47.76) * mm, "end": v(-68.5, -50.99) * mm});
            skLineSegment(sketch, "E847", {"start": v(-68.5, -50.99) * mm, "end": v(-66.99, -53.06) * mm});
            skLineSegment(sketch, "E848", {"start": v(-66.41, -47.53) * mm, "end": v(-63.72, -49.7) * mm});
            skLineSegment(sketch, "E849", {"start": v(-63.72, -49.7) * mm, "end": v(-61.29, -48.9) * mm});
            skLineSegment(sketch, "E850", {"start": v(-66.25, -47.02) * mm, "end": v(-62.8, -46.84) * mm});
            skLineSegment(sketch, "E851", {"start": v(-62.8, -46.84) * mm, "end": v(-61.29, -48.9) * mm});
            skLineSegment(sketch, "E852", {"start": v(-63.48, -42.2) * mm, "end": v(-63.48, -44.76) * mm});
            skLineSegment(sketch, "E853", {"start": v(-63.48, -44.76) * mm, "end": v(-66.37, -46.65) * mm});
            skLineSegment(sketch, "E854", {"start": v(-66.8, -46.34) * mm, "end": v(-65.9, -43) * mm});
            skLineSegment(sketch, "E855", {"start": v(-65.9, -43) * mm, "end": v(-63.48, -42.2) * mm});
            skArc(sketch, "E856", {"start": v(-67.58, -47.53) * mm, "mid": v(-67.44, -47.67) * mm, "end": v(-67.26, -47.76) * mm});
            skArc(sketch, "E857.trimOffspring", {"start": v(-67.63, -46.65) * mm, "mid": v(-67.71, -46.83) * mm, "end": v(-67.75, -47.02) * mm});
            skArc(sketch, "E858.trimOffspring", {"start": v(-66.8, -46.34) * mm, "mid": v(-67, -46.3) * mm, "end": v(-67.2, -46.34) * mm});
            skArc(sketch, "E859.trimOffspring", {"start": v(-66.25, -47.02) * mm, "mid": v(-66.28, -46.83) * mm, "end": v(-66.37, -46.65) * mm});
            skArc(sketch, "E860.trimOffspring", {"start": v(-66.73, -47.76) * mm, "mid": v(-66.55, -47.67) * mm, "end": v(-66.41, -47.53) * mm});
            skLineSegment(sketch, "E861", {"start": v(-69.72, -43.33) * mm, "end": v(-69.71, -44.18) * mm});
            skLineSegment(sketch, "E862", {"start": v(-69.71, -44.18) * mm, "end": v(-68.54, -44.94) * mm});
            skLineSegment(sketch, "E863", {"start": v(-68.54, -44.94) * mm, "end": v(-68.9, -43.6) * mm});
            skLineSegment(sketch, "E864", {"start": v(-68.9, -43.6) * mm, "end": v(-69.72, -43.33) * mm});
            skLineSegment(sketch, "E865", {"start": v(-64.29, -43.32) * mm, "end": v(-64.29, -44.17) * mm});
            skLineSegment(sketch, "E866", {"start": v(-64.29, -44.17) * mm, "end": v(-65.46, -44.94) * mm});
            skLineSegment(sketch, "E867", {"start": v(-65.46, -44.94) * mm, "end": v(-65.1, -43.59) * mm});
            skLineSegment(sketch, "E868", {"start": v(-65.1, -43.59) * mm, "end": v(-64.29, -43.32) * mm});
            skLineSegment(sketch, "E869", {"start": v(-66.99, -51.68) * mm, "end": v(-66.5, -50.99) * mm});
            skLineSegment(sketch, "E870", {"start": v(-66.5, -50.99) * mm, "end": v(-67, -49.68) * mm});
            skLineSegment(sketch, "E871", {"start": v(-67, -49.68) * mm, "end": v(-67.5, -50.99) * mm});
            skLineSegment(sketch, "E872", {"start": v(-67.5, -50.99) * mm, "end": v(-66.99, -51.68) * mm});
            skLineSegment(sketch, "E873", {"start": v(-62.6, -48.48) * mm, "end": v(-63.1, -47.8) * mm});
            skLineSegment(sketch, "E874", {"start": v(-63.1, -47.8) * mm, "end": v(-64.5, -47.86) * mm});
            skLineSegment(sketch, "E875", {"start": v(-64.5, -47.86) * mm, "end": v(-63.41, -48.74) * mm});
            skLineSegment(sketch, "E876", {"start": v(-63.41, -48.74) * mm, "end": v(-62.6, -48.48) * mm});
            skLineSegment(sketch, "E877", {"start": v(-71.39, -48.5) * mm, "end": v(-70.57, -48.75) * mm});
            skLineSegment(sketch, "E878", {"start": v(-70.57, -48.75) * mm, "end": v(-69.49, -47.87) * mm});
            skLineSegment(sketch, "E879", {"start": v(-69.49, -47.87) * mm, "end": v(-70.88, -47.8) * mm});
            skLineSegment(sketch, "E880", {"start": v(-70.88, -47.8) * mm, "end": v(-71.39, -48.5) * mm});
            skLineSegment(sketch, "E881", {"start": v(2.36, -53.88) * mm, "end": v(3.03, -56.35) * mm});
            skLineSegment(sketch, "E882", {"start": v(3.03, -56.35) * mm, "end": v(6.31, -57.42) * mm});
            skLineSegment(sketch, "E883", {"start": v(6.65, -57) * mm, "end": v(4.91, -54.02) * mm});
            skLineSegment(sketch, "E884", {"start": v(4.91, -54.02) * mm, "end": v(2.36, -53.88) * mm});
            skLineSegment(sketch, "E885", {"start": v(2, -60.93) * mm, "end": v(4.56, -61.05) * mm});
            skLineSegment(sketch, "E886", {"start": v(4.56, -61.05) * mm, "end": v(6.59, -58.26) * mm});
            skLineSegment(sketch, "E887", {"start": v(6.3, -57.8) * mm, "end": v(2.92, -58.54) * mm});
            skLineSegment(sketch, "E888", {"start": v(2.92, -58.54) * mm, "end": v(2, -60.93) * mm});
            skLineSegment(sketch, "E889", {"start": v(8.59, -63.44) * mm, "end": v(9.5, -61.05) * mm});
            skLineSegment(sketch, "E890", {"start": v(9.5, -61.05) * mm, "end": v(7.47, -58.26) * mm});
            skLineSegment(sketch, "E891", {"start": v(6.95, -58.4) * mm, "end": v(6.6, -61.83) * mm});
            skLineSegment(sketch, "E892", {"start": v(6.6, -61.83) * mm, "end": v(8.59, -63.44) * mm});
            skLineSegment(sketch, "E893", {"start": v(7.71, -57.95) * mm, "end": v(10.87, -59.35) * mm});
            skLineSegment(sketch, "E894", {"start": v(10.87, -59.35) * mm, "end": v(13.02, -57.95) * mm});
            skLineSegment(sketch, "E895", {"start": v(7.74, -57.42) * mm, "end": v(11.02, -56.35) * mm});
            skLineSegment(sketch, "E896", {"start": v(11.02, -56.35) * mm, "end": v(13.02, -57.95) * mm});
            skLineSegment(sketch, "E897", {"start": v(9.17, -52.05) * mm, "end": v(9.83, -54.52) * mm});
            skLineSegment(sketch, "E898", {"start": v(9.83, -54.52) * mm, "end": v(7.53, -57.1) * mm});
            skLineSegment(sketch, "E899", {"start": v(7.03, -56.9) * mm, "end": v(7.03, -53.45) * mm});
            skLineSegment(sketch, "E900", {"start": v(7.03, -53.45) * mm, "end": v(9.17, -52.05) * mm});
            skArc(sketch, "E901", {"start": v(6.59, -58.26) * mm, "mid": v(6.76, -58.35) * mm, "end": v(6.95, -58.4) * mm});
            skArc(sketch, "E902.trimOffspring", {"start": v(6.31, -57.42) * mm, "mid": v(6.28, -57.61) * mm, "end": v(6.3, -57.8) * mm});
            skArc(sketch, "E903.trimOffspring", {"start": v(7.03, -56.9) * mm, "mid": v(6.83, -56.93) * mm, "end": v(6.65, -57) * mm});
            skArc(sketch, "E904.trimOffspring", {"start": v(7.74, -57.42) * mm, "mid": v(7.65, -57.24) * mm, "end": v(7.53, -57.1) * mm});
            skArc(sketch, "E905.trimOffspring", {"start": v(7.47, -58.26) * mm, "mid": v(7.61, -58.12) * mm, "end": v(7.71, -57.95) * mm});
            skLineSegment(sketch, "E906", {"start": v(3.43, -54.75) * mm, "end": v(3.66, -55.57) * mm});
            skLineSegment(sketch, "E907", {"start": v(3.66, -55.57) * mm, "end": v(4.99, -56) * mm});
            skLineSegment(sketch, "E908", {"start": v(4.99, -56) * mm, "end": v(4.28, -54.8) * mm});
            skLineSegment(sketch, "E909", {"start": v(4.28, -54.8) * mm, "end": v(3.43, -54.75) * mm});
            skLineSegment(sketch, "E910", {"start": v(8.67, -53.34) * mm, "end": v(8.9, -54.16) * mm});
            skLineSegment(sketch, "E911", {"start": v(8.9, -54.16) * mm, "end": v(7.96, -55.2) * mm});
            skLineSegment(sketch, "E912", {"start": v(7.96, -55.2) * mm, "end": v(7.96, -53.8) * mm});
            skLineSegment(sketch, "E913", {"start": v(7.96, -53.8) * mm, "end": v(8.67, -53.34) * mm});
            skLineSegment(sketch, "E914", {"start": v(8.23, -62.1) * mm, "end": v(8.53, -61.31) * mm});
            skLineSegment(sketch, "E915", {"start": v(8.53, -61.31) * mm, "end": v(7.7, -60.18) * mm});
            skLineSegment(sketch, "E916", {"start": v(7.7, -60.18) * mm, "end": v(7.57, -61.57) * mm});
            skLineSegment(sketch, "E917", {"start": v(7.57, -61.57) * mm, "end": v(8.23, -62.1) * mm});
            skLineSegment(sketch, "E918", {"start": v(11.64, -57.88) * mm, "end": v(10.97, -57.35) * mm});
            skLineSegment(sketch, "E919", {"start": v(10.97, -57.35) * mm, "end": v(9.64, -57.78) * mm});
            skLineSegment(sketch, "E920", {"start": v(9.64, -57.78) * mm, "end": v(10.92, -58.35) * mm});
            skLineSegment(sketch, "E921", {"start": v(10.92, -58.35) * mm, "end": v(11.64, -57.88) * mm});
            skLineSegment(sketch, "E922", {"start": v(3.16, -60.17) * mm, "end": v(4, -60.21) * mm});
            skLineSegment(sketch, "E923", {"start": v(4, -60.21) * mm, "end": v(4.83, -59.08) * mm});
            skLineSegment(sketch, "E924", {"start": v(4.83, -59.08) * mm, "end": v(3.46, -59.38) * mm});
            skLineSegment(sketch, "E925", {"start": v(3.46, -59.38) * mm, "end": v(3.16, -60.17) * mm});
            skLineSegment(sketch, "E926", {"start": v(79.46, 7.04) * mm, "end": v(80.13, 4.58) * mm});
            skLineSegment(sketch, "E927", {"start": v(80.13, 4.58) * mm, "end": v(83.41, 3.5) * mm});
            skLineSegment(sketch, "E928", {"start": v(83.75, 3.92) * mm, "end": v(82.01, 6.9) * mm});
            skLineSegment(sketch, "E929", {"start": v(82.01, 6.9) * mm, "end": v(79.46, 7.04) * mm});
            skLineSegment(sketch, "E930", {"start": v(79.1, 0) * mm, "end": v(81.65, -0.12) * mm});
            skLineSegment(sketch, "E931", {"start": v(81.65, -0.12) * mm, "end": v(83.68, 2.67) * mm});
            skLineSegment(sketch, "E932", {"start": v(83.4, 3.12) * mm, "end": v(80.02, 2.39) * mm});
            skLineSegment(sketch, "E933", {"start": v(80.02, 2.39) * mm, "end": v(79.1, 0) * mm});
            skLineSegment(sketch, "E934", {"start": v(85.69, -2.52) * mm, "end": v(86.6, -0.12) * mm});
            skLineSegment(sketch, "E935", {"start": v(86.6, -0.12) * mm, "end": v(84.57, 2.67) * mm});
            skLineSegment(sketch, "E936", {"start": v(84.05, 2.53) * mm, "end": v(83.7, -0.9) * mm});
            skLineSegment(sketch, "E937", {"start": v(83.7, -0.9) * mm, "end": v(85.69, -2.52) * mm});
            skLineSegment(sketch, "E938", {"start": v(84.81, 2.97) * mm, "end": v(87.97, 1.58) * mm});
            skLineSegment(sketch, "E939", {"start": v(87.97, 1.58) * mm, "end": v(90.12, 2.97) * mm});
            skLineSegment(sketch, "E940", {"start": v(84.84, 3.5) * mm, "end": v(88.12, 4.58) * mm});
            skLineSegment(sketch, "E941", {"start": v(88.12, 4.58) * mm, "end": v(90.12, 2.97) * mm});
            skLineSegment(sketch, "E942", {"start": v(86.27, 8.88) * mm, "end": v(86.93, 6.4) * mm});
            skLineSegment(sketch, "E943", {"start": v(86.93, 6.4) * mm, "end": v(84.63, 3.84) * mm});
            skLineSegment(sketch, "E944", {"start": v(84.13, 4.03) * mm, "end": v(84.13, 7.48) * mm});
            skLineSegment(sketch, "E945", {"start": v(84.13, 7.48) * mm, "end": v(86.27, 8.88) * mm});
            skArc(sketch, "E946", {"start": v(83.68, 2.67) * mm, "mid": v(83.86, 2.58) * mm, "end": v(84.05, 2.53) * mm});
            skArc(sketch, "E947.trimOffspring", {"start": v(83.41, 3.5) * mm, "mid": v(83.38, 3.31) * mm, "end": v(83.4, 3.12) * mm});
            skArc(sketch, "E948.trimOffspring", {"start": v(84.13, 4.03) * mm, "mid": v(83.93, 4) * mm, "end": v(83.75, 3.92) * mm});
            skArc(sketch, "E949.trimOffspring", {"start": v(84.84, 3.5) * mm, "mid": v(84.75, 3.69) * mm, "end": v(84.63, 3.84) * mm});
            skArc(sketch, "E950.trimOffspring", {"start": v(84.57, 2.67) * mm, "mid": v(84.7, 2.8) * mm, "end": v(84.81, 2.97) * mm});
            skLineSegment(sketch, "E951", {"start": v(80.53, 6.18) * mm, "end": v(80.76, 5.35) * mm});
            skLineSegment(sketch, "E952", {"start": v(80.76, 5.35) * mm, "end": v(82.09, 4.92) * mm});
            skLineSegment(sketch, "E953", {"start": v(82.09, 4.92) * mm, "end": v(81.38, 6.13) * mm});
            skLineSegment(sketch, "E954", {"start": v(81.38, 6.13) * mm, "end": v(80.53, 6.18) * mm});
            skLineSegment(sketch, "E955", {"start": v(85.77, 7.6) * mm, "end": v(86, 6.77) * mm});
            skLineSegment(sketch, "E956", {"start": v(86, 6.77) * mm, "end": v(85.06, 5.72) * mm});
            skLineSegment(sketch, "E957", {"start": v(85.06, 5.72) * mm, "end": v(85.06, 7.12) * mm});
            skLineSegment(sketch, "E958", {"start": v(85.06, 7.12) * mm, "end": v(85.77, 7.6) * mm});
            skLineSegment(sketch, "E959", {"start": v(85.33, -1.18) * mm, "end": v(85.63, -0.39) * mm});
            skLineSegment(sketch, "E960", {"start": v(85.63, -0.39) * mm, "end": v(84.8, 0.75) * mm});
            skLineSegment(sketch, "E961", {"start": v(84.8, 0.75) * mm, "end": v(84.67, -0.65) * mm});
            skLineSegment(sketch, "E962", {"start": v(84.67, -0.65) * mm, "end": v(85.33, -1.18) * mm});
            skLineSegment(sketch, "E963", {"start": v(88.74, 3.04) * mm, "end": v(88.07, 3.58) * mm});
            skLineSegment(sketch, "E964", {"start": v(88.07, 3.58) * mm, "end": v(86.74, 3.14) * mm});
            skLineSegment(sketch, "E965", {"start": v(86.74, 3.14) * mm, "end": v(88.02, 2.58) * mm});
            skLineSegment(sketch, "E966", {"start": v(88.02, 2.58) * mm, "end": v(88.74, 3.04) * mm});
            skLineSegment(sketch, "E967", {"start": v(80.26, 0.75) * mm, "end": v(81.1, 0.71) * mm});
            skLineSegment(sketch, "E968", {"start": v(81.1, 0.71) * mm, "end": v(81.93, 1.85) * mm});
            skLineSegment(sketch, "E969", {"start": v(81.93, 1.85) * mm, "end": v(80.56, 1.55) * mm});
            skLineSegment(sketch, "E970", {"start": v(80.56, 1.55) * mm, "end": v(80.26, 0.75) * mm});
            skSolve(sketch);
        }
        {
            var Q0;
            Q0=qCreatedBy(makeId("Right.planeOp"),FACE);
            var sketch = newSketch(context, id + "F3", { "sketchPlane" : qUnion([Q0])});
            skLineSegment(sketch, "E971", {"start": v(0, -70.92) * mm, "end": v(0, 69.35) * mm, "construction": true});
            skSolve(sketch);
        }
        {
            var Q0;
            Q0=makeQuery(id+"F1.opExtrude","CAP_FACE",FACE,{"disambiguationData":[OSD([sQuery(id+"F0.wireOp",EDGE,"E0.bottom"),sQuery(id+"F0.wireOp",EDGE,"E0.top"),sQuery(id+"F0.wireOp",EDGE,"E0.left"),sQuery(id+"F0.wireOp",EDGE,"E0.right"),sQuery(id+"F0.wireOp",EDGE,"E1"),sQuery(id+"F0.wireOp",EDGE,"E2"),sQuery(id+"F0.wireOp",EDGE,"E3"),sQuery(id+"F0.wireOp",EDGE,"E4.MirrorCS"),sQuery(id+"F0.wireOp",EDGE,"E5.MirrorCS"),sQuery(id+"F0.wireOp",EDGE,"E6.MirrorCS"),sQuery(id+"F0.wireOp",EDGE,"E7.MirrorCS"),sQuery(id+"F0.wireOp",EDGE,"E8.MirrorCS"),sQuery(id+"F0.wireOp",EDGE,"E9.trimOffspring"),sQuery(id+"F0.wireOp",EDGE,"E10.trimOffspring"),sQuery(id+"F0.wireOp",EDGE,"E11.trimOffspring"),sQuery(id+"F0.wireOp",EDGE,"E12.trimOffspring")])],"isStart":false});
            var sketch = newSketch(context, id + "F4", { "sketchPlane" : qUnion([Q0])});
            skLineSegment(sketch, "E972.bottom", {"start": v(-50.8, 38.1) * mm, "end": v(50.8, 38.1) * mm});
            skLineSegment(sketch, "E972.top", {"start": v(-50.8, -38.1) * mm, "end": v(50.8, -38.1) * mm});
            skLineSegment(sketch, "E972.left", {"start": v(-50.8, 38.1) * mm, "end": v(-50.8, -38.1) * mm});
            skLineSegment(sketch, "E972.right", {"start": v(50.8, 38.1) * mm, "end": v(50.8, -38.1) * mm});
            skSolve(sketch);
        }
        {
            var Q0;
            Q0=makeQuery(id+"F4.imprint","IMPRINT",FACE,{"disambiguationData":[TD([[makeQuery(id+"F4.imprint","IMPRINT",EDGE,{"derivedFrom":sQuery(id+"F4.wireOp",EDGE,"E972.bottom")}),-1.0]])]});
            extrude(context, id + "F5", {"entities" : qUnion([Q0]), "operationType" : NewBodyOperationType.REMOVE, "endBound" : BoundingType.THROUGH_ALL, "oppositeDirection" : true, "depth" : 5 * mm});
        }
        {
            var Q0;
            Q0=qSketchRegion(id+"F2",true);
            extrude(context, id + "F6", {"entities" : qUnion([Q0]), "operationType" : NewBodyOperationType.ADD, "depth" : 2 * mm});
        }
        {
            var Q0;
            {var subQ0=sQuery(id+"F0.wireOp",EDGE,"E3");var subQ1=sQuery(id+"F0.wireOp",EDGE,"E0.bottom");var subQ2=sQuery(id+"F0.wireOp",EDGE,"E6.MirrorCS");var subQ3=sQuery(id+"F0.wireOp",EDGE,"E7.MirrorCS");var subQ4=sQuery(id+"F0.wireOp",EDGE,"E8.MirrorCS");var subQ5=sQuery(id+"F0.wireOp",EDGE,"E9.trimOffspring");var subQ6=sQuery(id+"F0.wireOp",EDGE,"E10.trimOffspring");var subQ7=sQuery(id+"F0.wireOp",EDGE,"E11.trimOffspring");var subQ8=sQuery(id+"F0.wireOp",EDGE,"E12.trimOffspring");var subQ9=sQuery(id+"F0.wireOp",EDGE,"E0.top");var subQ10=sQuery(id+"F0.wireOp",EDGE,"E0.left");var subQ11=sQuery(id+"F0.wireOp",EDGE,"E0.right");var subQ12=sQuery(id+"F0.wireOp",EDGE,"E1");var subQ13=sQuery(id+"F0.wireOp",EDGE,"E2");var subQ14=sQuery(id+"F0.wireOp",EDGE,"E4.MirrorCS");var subQ15=sQuery(id+"F0.wireOp",EDGE,"E5.MirrorCS");Q0=makeQuery(id+"F6.boolean.opBoolean","SPLIT",FACE,{"disambiguationData":[TD([makeQuery(id+"F1.opExtrude","SWEPT_FACE",FACE,{"disambiguationData":[OSD([subQ1])]})])],"derivedFrom":makeQuery(id+"F1.opExtrude","CAP_FACE",FACE,{"disambiguationData":[OSD([subQ1,subQ9,subQ10,subQ11,subQ12,subQ13,subQ0,subQ14,subQ15,subQ2,subQ3,subQ4,subQ5,subQ6,subQ7,subQ8])],"isStart":false})});}
            var sketch = newSketch(context, id + "F7", { "sketchPlane" : qUnion([Q0])});
            skText(sketch, "E973", { "text": "          I LOVE YOU GG!\nMY FIRST CHRISTMAS - 2016", "fontName": "OpenSans-BoldItalic.ttf"});
            const initialGuessF7  = {"E973": [-0.05829, 0.0425, 0, -1, 0.00473]};
            skSetInitialGuess(sketch, initialGuessF7);
            skSolve(sketch);
        }
        {
            var Q0;
            Q0=qSketchRegion(id+"F7",true);
            extrude(context, id + "F8", {"entities" : qUnion([Q0]), "operationType" : NewBodyOperationType.ADD, "depth" : 2 * mm});
        }
        {
            var Q0;
            {var subQ240=sQuery(id+"F0.wireOp",EDGE,"E5.MirrorCS");var subQ244=sQuery(id+"F0.wireOp",EDGE,"E4.MirrorCS");var subQ248=sQuery(id+"F0.wireOp",EDGE,"E2");var subQ251=sQuery(id+"F0.wireOp",EDGE,"E1");var subQ254=sQuery(id+"F0.wireOp",EDGE,"E0.right");var subQ257=sQuery(id+"F0.wireOp",EDGE,"E0.left");var subQ260=sQuery(id+"F0.wireOp",EDGE,"E0.top");var subQ313=sQuery(id+"F0.wireOp",EDGE,"E12.trimOffspring");var subQ320=sQuery(id+"F0.wireOp",EDGE,"E11.trimOffspring");var subQ330=sQuery(id+"F0.wireOp",EDGE,"E10.trimOffspring");var subQ338=sQuery(id+"F0.wireOp",EDGE,"E9.trimOffspring");var subQ346=sQuery(id+"F0.wireOp",EDGE,"E8.MirrorCS");var subQ354=sQuery(id+"F0.wireOp",EDGE,"E7.MirrorCS");var subQ362=sQuery(id+"F0.wireOp",EDGE,"E6.MirrorCS");var subQ383=sQuery(id+"F0.wireOp",EDGE,"E0.bottom");var subQ384=makeQuery(id+"F1.opExtrude","SWEPT_FACE",FACE,{"disambiguationData":[OSD([subQ383])]});var subQ406=sQuery(id+"F0.wireOp",EDGE,"E3");Q0=makeQuery(id+"F8.boolean.opBoolean","SPLIT",FACE,{"disambiguationData":[TD([subQ384])],"derivedFrom":makeQuery(id+"F6.boolean.opBoolean","SPLIT",FACE,{"disambiguationData":[TD([subQ384])],"derivedFrom":makeQuery(id+"F1.opExtrude","CAP_FACE",FACE,{"disambiguationData":[OSD([subQ383,subQ260,subQ257,subQ254,subQ251,subQ248,subQ406,subQ244,subQ240,subQ362,subQ354,subQ346,subQ338,subQ330,subQ320,subQ313])],"isStart":false})})});}
            var sketch = newSketch(context, id + "F9", { "sketchPlane" : qUnion([Q0])});
            skLineSegment(sketch, "E974.0.0", {"start": v(-50, 37.5) * mm, "end": v(-50, -37.5) * mm});
            skLineSegment(sketch, "E974.0.1", {"start": v(-50, -37.5) * mm, "end": v(50, -37.5) * mm});
            skLineSegment(sketch, "E974.0.2", {"start": v(50, -37.5) * mm, "end": v(50, 37.5) * mm});
            skLineSegment(sketch, "E974.0.3", {"start": v(50, 37.5) * mm, "end": v(-50, 37.5) * mm});
            skLineSegment(sketch, "E975.bottom", {"start": v(47.5, 35) * mm, "end": v(-47.5, 35) * mm});
            skLineSegment(sketch, "E975.top", {"start": v(47.5, -35) * mm, "end": v(-47.5, -35) * mm});
            skLineSegment(sketch, "E975.left", {"start": v(47.5, 35) * mm, "end": v(47.5, -35) * mm});
            skLineSegment(sketch, "E975.right", {"start": v(-47.5, 35) * mm, "end": v(-47.5, -35) * mm});
            skPoint(sketch, "E975.middle", {"position": v(0, 0) * mm});
            skSolve(sketch);
        }
        {
            var Q0;
            Q0 = qSketchRegion(id + "F9", true);
            extrude(context, id + "F10", {"entities" : qUnion([Q0]), "operationType" : NewBodyOperationType.ADD, "oppositeDirection" : true, "depth" : 2 * mm});
        }
    });
